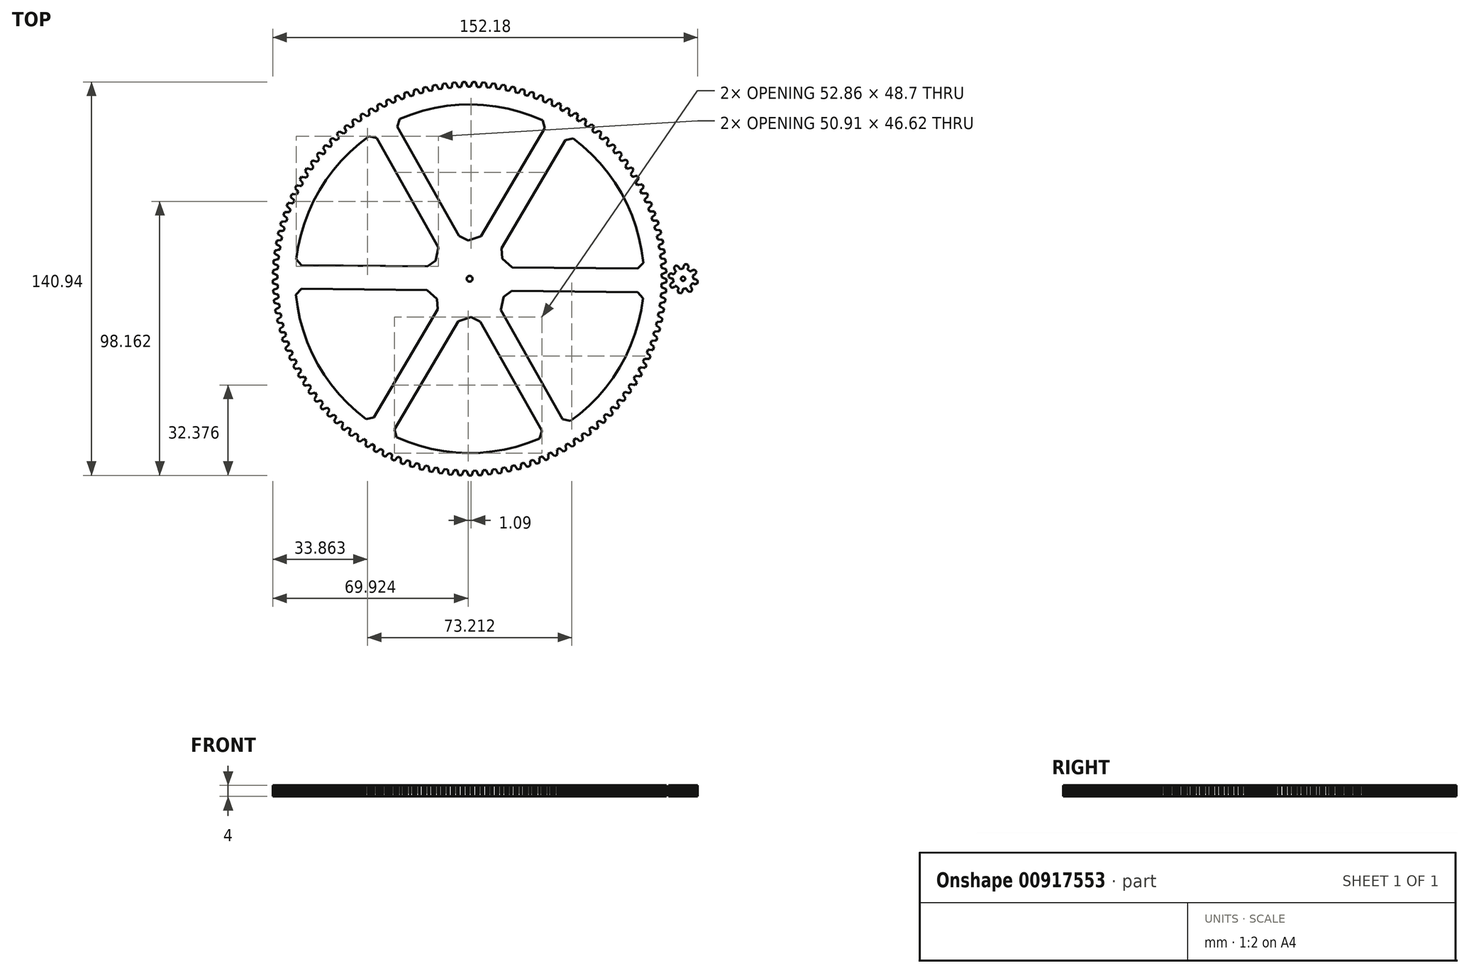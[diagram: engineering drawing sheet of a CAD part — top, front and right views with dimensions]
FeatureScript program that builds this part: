
annotation { "Feature Type Name" : "Feature", "Feature Type Description" : "" }
export const myFeature = defineFeature(function(context is Context, id is Id, definition is map)
    precondition{}
    {
        {
            var Q0;
            Q0=qCreatedBy(makeId("Top.planeOp"),FACE);
            var sketch = newSketch(context, id + "F0", { "sketchPlane" : qUnion([Q0])});
            skLineSegment(sketch, "E0", {"start": v(63.17, 0.46) * mm, "end": v(63.59, 0.33) * mm});
            skLineSegment(sketch, "E1", {"start": v(63.59, 0.33) * mm, "end": v(64.43, 0.02) * mm});
            skLineSegment(sketch, "E2", {"start": v(64.43, 0.02) * mm, "end": v(64.85, -0.14) * mm});
            skLineSegment(sketch, "E3", {"start": v(64.85, -0.14) * mm, "end": v(64.84, -1.27) * mm});
            skLineSegment(sketch, "E4", {"start": v(64.84, -1.27) * mm, "end": v(64.41, -1.42) * mm});
            skLineSegment(sketch, "E5", {"start": v(64.41, -1.42) * mm, "end": v(63.57, -1.71) * mm});
            skLineSegment(sketch, "E6", {"start": v(63.57, -1.71) * mm, "end": v(63.14, -1.84) * mm});
            skLineSegment(sketch, "E7", {"start": v(63.14, -1.84) * mm, "end": v(63.1, -3) * mm});
            skLineSegment(sketch, "E8", {"start": v(63.1, -3) * mm, "end": v(63.52, -3.15) * mm});
            skLineSegment(sketch, "E9", {"start": v(63.52, -3.15) * mm, "end": v(64.34, -3.5) * mm});
            skLineSegment(sketch, "E10", {"start": v(64.34, -3.5) * mm, "end": v(64.75, -3.68) * mm});
            skLineSegment(sketch, "E11", {"start": v(64.75, -3.68) * mm, "end": v(64.68, -4.8) * mm});
            skLineSegment(sketch, "E12", {"start": v(64.68, -4.8) * mm, "end": v(64.25, -4.94) * mm});
            skLineSegment(sketch, "E13", {"start": v(64.25, -4.94) * mm, "end": v(63.4, -5.18) * mm});
            skLineSegment(sketch, "E14", {"start": v(63.4, -5.18) * mm, "end": v(62.97, -5.3) * mm});
            skLineSegment(sketch, "E15", {"start": v(62.97, -5.3) * mm, "end": v(62.87, -6.44) * mm});
            skLineSegment(sketch, "E16", {"start": v(62.87, -6.44) * mm, "end": v(63.27, -6.62) * mm});
            skLineSegment(sketch, "E17", {"start": v(63.27, -6.62) * mm, "end": v(64.08, -7) * mm});
            skLineSegment(sketch, "E18", {"start": v(64.08, -7) * mm, "end": v(64.48, -7.21) * mm});
            skLineSegment(sketch, "E19", {"start": v(64.48, -7.21) * mm, "end": v(64.35, -8.33) * mm});
            skLineSegment(sketch, "E20", {"start": v(64.35, -8.33) * mm, "end": v(63.92, -8.45) * mm});
            skLineSegment(sketch, "E21", {"start": v(63.92, -8.45) * mm, "end": v(63.05, -8.65) * mm});
            skLineSegment(sketch, "E22", {"start": v(63.05, -8.65) * mm, "end": v(62.61, -8.73) * mm});
            skLineSegment(sketch, "E23", {"start": v(62.61, -8.73) * mm, "end": v(62.46, -9.88) * mm});
            skLineSegment(sketch, "E24", {"start": v(62.46, -9.88) * mm, "end": v(62.85, -10.08) * mm});
            skLineSegment(sketch, "E25", {"start": v(62.85, -10.08) * mm, "end": v(63.64, -10.5) * mm});
            skLineSegment(sketch, "E26", {"start": v(63.64, -10.5) * mm, "end": v(64.03, -10.73) * mm});
            skLineSegment(sketch, "E27", {"start": v(64.03, -10.73) * mm, "end": v(63.85, -11.84) * mm});
            skLineSegment(sketch, "E28", {"start": v(63.85, -11.84) * mm, "end": v(63.4, -11.93) * mm});
            skLineSegment(sketch, "E29", {"start": v(63.4, -11.93) * mm, "end": v(62.53, -12.08) * mm});
            skLineSegment(sketch, "E30", {"start": v(62.53, -12.08) * mm, "end": v(62.09, -12.15) * mm});
            skLineSegment(sketch, "E31", {"start": v(62.09, -12.15) * mm, "end": v(61.87, -13.28) * mm});
            skLineSegment(sketch, "E32", {"start": v(61.87, -13.28) * mm, "end": v(62.26, -13.5) * mm});
            skLineSegment(sketch, "E33", {"start": v(62.26, -13.5) * mm, "end": v(63.02, -13.97) * mm});
            skLineSegment(sketch, "E34", {"start": v(63.02, -13.97) * mm, "end": v(63.4, -14.21) * mm});
            skLineSegment(sketch, "E35", {"start": v(63.4, -14.21) * mm, "end": v(63.16, -15.31) * mm});
            skLineSegment(sketch, "E36", {"start": v(63.16, -15.31) * mm, "end": v(62.72, -15.38) * mm});
            skLineSegment(sketch, "E37", {"start": v(62.72, -15.38) * mm, "end": v(61.83, -15.5) * mm});
            skLineSegment(sketch, "E38", {"start": v(61.83, -15.5) * mm, "end": v(61.4, -15.54) * mm});
            skLineSegment(sketch, "E39", {"start": v(61.4, -15.54) * mm, "end": v(61.12, -16.66) * mm});
            skLineSegment(sketch, "E40", {"start": v(61.12, -16.66) * mm, "end": v(61.5, -16.9) * mm});
            skLineSegment(sketch, "E41", {"start": v(61.5, -16.9) * mm, "end": v(62.23, -17.4) * mm});
            skLineSegment(sketch, "E42", {"start": v(62.23, -17.4) * mm, "end": v(62.6, -17.66) * mm});
            skLineSegment(sketch, "E43", {"start": v(62.6, -17.66) * mm, "end": v(62.3, -18.75) * mm});
            skLineSegment(sketch, "E44", {"start": v(62.3, -18.75) * mm, "end": v(61.86, -18.8) * mm});
            skLineSegment(sketch, "E45", {"start": v(61.86, -18.8) * mm, "end": v(60.97, -18.86) * mm});
            skLineSegment(sketch, "E46", {"start": v(60.97, -18.86) * mm, "end": v(60.53, -18.88) * mm});
            skLineSegment(sketch, "E47", {"start": v(60.53, -18.88) * mm, "end": v(60.2, -20) * mm});
            skLineSegment(sketch, "E48", {"start": v(60.2, -20) * mm, "end": v(60.56, -20.25) * mm});
            skLineSegment(sketch, "E49", {"start": v(60.56, -20.25) * mm, "end": v(61.27, -20.79) * mm});
            skLineSegment(sketch, "E50", {"start": v(61.27, -20.79) * mm, "end": v(61.62, -21.07) * mm});
            skLineSegment(sketch, "E51", {"start": v(61.62, -21.07) * mm, "end": v(61.28, -22.14) * mm});
            skLineSegment(sketch, "E52", {"start": v(61.28, -22.14) * mm, "end": v(60.83, -22.16) * mm});
            skLineSegment(sketch, "E53", {"start": v(60.83, -22.16) * mm, "end": v(59.94, -22.19) * mm});
            skLineSegment(sketch, "E54", {"start": v(59.94, -22.19) * mm, "end": v(59.5, -22.18) * mm});
            skLineSegment(sketch, "E55", {"start": v(59.5, -22.18) * mm, "end": v(59.11, -23.27) * mm});
            skLineSegment(sketch, "E56", {"start": v(59.11, -23.27) * mm, "end": v(59.46, -23.55) * mm});
            skLineSegment(sketch, "E57", {"start": v(59.46, -23.55) * mm, "end": v(60.14, -24.12) * mm});
            skLineSegment(sketch, "E58", {"start": v(60.14, -24.12) * mm, "end": v(60.48, -24.42) * mm});
            skLineSegment(sketch, "E59", {"start": v(60.48, -24.42) * mm, "end": v(60.08, -25.47) * mm});
            skLineSegment(sketch, "E60", {"start": v(60.08, -25.47) * mm, "end": v(59.63, -25.47) * mm});
            skLineSegment(sketch, "E61", {"start": v(59.63, -25.47) * mm, "end": v(58.74, -25.45) * mm});
            skLineSegment(sketch, "E62", {"start": v(58.74, -25.45) * mm, "end": v(58.3, -25.43) * mm});
            skLineSegment(sketch, "E63", {"start": v(58.3, -25.43) * mm, "end": v(57.86, -26.5) * mm});
            skLineSegment(sketch, "E64", {"start": v(57.86, -26.5) * mm, "end": v(58.2, -26.79) * mm});
            skLineSegment(sketch, "E65", {"start": v(58.2, -26.79) * mm, "end": v(58.85, -27.4) * mm});
            skLineSegment(sketch, "E66", {"start": v(58.85, -27.4) * mm, "end": v(59.17, -27.71) * mm});
            skLineSegment(sketch, "E67", {"start": v(59.17, -27.71) * mm, "end": v(58.72, -28.74) * mm});
            skLineSegment(sketch, "E68", {"start": v(58.72, -28.74) * mm, "end": v(58.27, -28.72) * mm});
            skLineSegment(sketch, "E69", {"start": v(58.27, -28.72) * mm, "end": v(57.38, -28.65) * mm});
            skLineSegment(sketch, "E70", {"start": v(57.38, -28.65) * mm, "end": v(56.94, -28.6) * mm});
            skLineSegment(sketch, "E71", {"start": v(56.94, -28.6) * mm, "end": v(56.45, -29.65) * mm});
            skLineSegment(sketch, "E72", {"start": v(56.45, -29.65) * mm, "end": v(56.77, -29.96) * mm});
            skLineSegment(sketch, "E73", {"start": v(56.77, -29.96) * mm, "end": v(57.4, -30.6) * mm});
            skLineSegment(sketch, "E74", {"start": v(57.4, -30.6) * mm, "end": v(57.7, -30.93) * mm});
            skLineSegment(sketch, "E75", {"start": v(57.7, -30.93) * mm, "end": v(57.2, -31.94) * mm});
            skLineSegment(sketch, "E76", {"start": v(57.2, -31.94) * mm, "end": v(56.75, -31.9) * mm});
            skLineSegment(sketch, "E77", {"start": v(56.75, -31.9) * mm, "end": v(55.86, -31.78) * mm});
            skLineSegment(sketch, "E78", {"start": v(55.86, -31.78) * mm, "end": v(55.42, -31.71) * mm});
            skLineSegment(sketch, "E79", {"start": v(55.42, -31.71) * mm, "end": v(54.88, -32.73) * mm});
            skLineSegment(sketch, "E80", {"start": v(54.88, -32.73) * mm, "end": v(55.18, -33.06) * mm});
            skLineSegment(sketch, "E81", {"start": v(55.18, -33.06) * mm, "end": v(55.77, -33.73) * mm});
            skLineSegment(sketch, "E82", {"start": v(55.77, -33.73) * mm, "end": v(56.06, -34.07) * mm});
            skLineSegment(sketch, "E83", {"start": v(56.06, -34.07) * mm, "end": v(55.5, -35.05) * mm});
            skLineSegment(sketch, "E84", {"start": v(55.5, -35.05) * mm, "end": v(55.06, -34.99) * mm});
            skLineSegment(sketch, "E85", {"start": v(55.06, -34.99) * mm, "end": v(54.18, -34.83) * mm});
            skLineSegment(sketch, "E86", {"start": v(54.18, -34.83) * mm, "end": v(53.75, -34.74) * mm});
            skLineSegment(sketch, "E87", {"start": v(53.75, -34.74) * mm, "end": v(53.16, -35.73) * mm});
            skLineSegment(sketch, "E88", {"start": v(53.16, -35.73) * mm, "end": v(53.45, -36.07) * mm});
            skLineSegment(sketch, "E89", {"start": v(53.45, -36.07) * mm, "end": v(54, -36.77) * mm});
            skLineSegment(sketch, "E90", {"start": v(54, -36.77) * mm, "end": v(54.27, -37.13) * mm});
            skLineSegment(sketch, "E91", {"start": v(54.27, -37.13) * mm, "end": v(53.67, -38.08) * mm});
            skLineSegment(sketch, "E92", {"start": v(53.67, -38.08) * mm, "end": v(53.23, -38) * mm});
            skLineSegment(sketch, "E93", {"start": v(53.23, -38) * mm, "end": v(52.36, -37.8) * mm});
            skLineSegment(sketch, "E94", {"start": v(52.36, -37.8) * mm, "end": v(51.93, -37.68) * mm});
            skLineSegment(sketch, "E95", {"start": v(51.93, -37.68) * mm, "end": v(51.3, -38.64) * mm});
            skLineSegment(sketch, "E96", {"start": v(51.3, -38.64) * mm, "end": v(51.56, -39) * mm});
            skLineSegment(sketch, "E97", {"start": v(51.56, -39) * mm, "end": v(52.08, -39.72) * mm});
            skLineSegment(sketch, "E98", {"start": v(52.08, -39.72) * mm, "end": v(52.33, -40.1) * mm});
            skLineSegment(sketch, "E99", {"start": v(52.33, -40.1) * mm, "end": v(51.68, -41.01) * mm});
            skLineSegment(sketch, "E100", {"start": v(51.68, -41.01) * mm, "end": v(51.25, -40.9) * mm});
            skLineSegment(sketch, "E101", {"start": v(51.25, -40.9) * mm, "end": v(50.39, -40.66) * mm});
            skLineSegment(sketch, "E102", {"start": v(50.39, -40.66) * mm, "end": v(49.96, -40.52) * mm});
            skLineSegment(sketch, "E103", {"start": v(49.96, -40.52) * mm, "end": v(49.28, -41.45) * mm});
            skLineSegment(sketch, "E104", {"start": v(49.28, -41.45) * mm, "end": v(49.53, -41.82) * mm});
            skLineSegment(sketch, "E105", {"start": v(49.53, -41.82) * mm, "end": v(50, -42.57) * mm});
            skLineSegment(sketch, "E106", {"start": v(50, -42.57) * mm, "end": v(50.24, -42.95) * mm});
            skLineSegment(sketch, "E107", {"start": v(50.24, -42.95) * mm, "end": v(49.55, -43.84) * mm});
            skLineSegment(sketch, "E108", {"start": v(49.55, -43.84) * mm, "end": v(49.12, -43.7) * mm});
            skLineSegment(sketch, "E109", {"start": v(49.12, -43.7) * mm, "end": v(48.27, -43.42) * mm});
            skLineSegment(sketch, "E110", {"start": v(48.27, -43.42) * mm, "end": v(47.86, -43.27) * mm});
            skLineSegment(sketch, "E111", {"start": v(47.86, -43.27) * mm, "end": v(47.12, -44.16) * mm});
            skLineSegment(sketch, "E112", {"start": v(47.12, -44.16) * mm, "end": v(47.36, -44.53) * mm});
            skLineSegment(sketch, "E113", {"start": v(47.36, -44.53) * mm, "end": v(47.8, -45.3) * mm});
            skLineSegment(sketch, "E114", {"start": v(47.8, -45.3) * mm, "end": v(48.01, -45.7) * mm});
            skLineSegment(sketch, "E115", {"start": v(48.01, -45.7) * mm, "end": v(47.28, -46.56) * mm});
            skLineSegment(sketch, "E116", {"start": v(47.28, -46.56) * mm, "end": v(46.85, -46.4) * mm});
            skLineSegment(sketch, "E117", {"start": v(46.85, -46.4) * mm, "end": v(46.02, -46.07) * mm});
            skLineSegment(sketch, "E118", {"start": v(46.02, -46.07) * mm, "end": v(45.62, -45.9) * mm});
            skLineSegment(sketch, "E119", {"start": v(45.62, -45.9) * mm, "end": v(44.84, -46.75) * mm});
            skLineSegment(sketch, "E120", {"start": v(44.84, -46.75) * mm, "end": v(45.05, -47.14) * mm});
            skLineSegment(sketch, "E121", {"start": v(45.05, -47.14) * mm, "end": v(45.46, -47.94) * mm});
            skLineSegment(sketch, "E122", {"start": v(45.46, -47.94) * mm, "end": v(45.65, -48.34) * mm});
            skLineSegment(sketch, "E123", {"start": v(45.65, -48.34) * mm, "end": v(44.87, -49.16) * mm});
            skLineSegment(sketch, "E124", {"start": v(44.87, -49.16) * mm, "end": v(44.46, -48.98) * mm});
            skLineSegment(sketch, "E125", {"start": v(44.46, -48.98) * mm, "end": v(43.64, -48.6) * mm});
            skLineSegment(sketch, "E126", {"start": v(43.64, -48.6) * mm, "end": v(43.25, -48.41) * mm});
            skLineSegment(sketch, "E127", {"start": v(43.25, -48.41) * mm, "end": v(42.43, -49.23) * mm});
            skLineSegment(sketch, "E128", {"start": v(42.43, -49.23) * mm, "end": v(42.62, -49.63) * mm});
            skLineSegment(sketch, "E129", {"start": v(42.62, -49.63) * mm, "end": v(42.98, -50.44) * mm});
            skLineSegment(sketch, "E130", {"start": v(42.98, -50.44) * mm, "end": v(43.16, -50.86) * mm});
            skLineSegment(sketch, "E131", {"start": v(43.16, -50.86) * mm, "end": v(42.34, -51.63) * mm});
            skLineSegment(sketch, "E132", {"start": v(42.34, -51.63) * mm, "end": v(41.93, -51.43) * mm});
            skLineSegment(sketch, "E133", {"start": v(41.93, -51.43) * mm, "end": v(41.14, -51.02) * mm});
            skLineSegment(sketch, "E134", {"start": v(41.14, -51.02) * mm, "end": v(40.75, -50.8) * mm});
            skLineSegment(sketch, "E135", {"start": v(40.75, -50.8) * mm, "end": v(39.9, -51.58) * mm});
            skLineSegment(sketch, "E136", {"start": v(39.9, -51.58) * mm, "end": v(40.06, -51.99) * mm});
            skLineSegment(sketch, "E137", {"start": v(40.06, -51.99) * mm, "end": v(40.39, -52.82) * mm});
            skLineSegment(sketch, "E138", {"start": v(40.39, -52.82) * mm, "end": v(40.54, -53.24) * mm});
            skLineSegment(sketch, "E139", {"start": v(40.54, -53.24) * mm, "end": v(39.68, -53.97) * mm});
            skLineSegment(sketch, "E140", {"start": v(39.68, -53.97) * mm, "end": v(39.29, -53.76) * mm});
            skLineSegment(sketch, "E141", {"start": v(39.29, -53.76) * mm, "end": v(38.52, -53.3) * mm});
            skLineSegment(sketch, "E142", {"start": v(38.52, -53.3) * mm, "end": v(38.14, -53.07) * mm});
            skLineSegment(sketch, "E143", {"start": v(38.14, -53.07) * mm, "end": v(37.24, -53.8) * mm});
            skLineSegment(sketch, "E144", {"start": v(37.24, -53.8) * mm, "end": v(37.4, -54.22) * mm});
            skLineSegment(sketch, "E145", {"start": v(37.4, -54.22) * mm, "end": v(37.67, -55.06) * mm});
            skLineSegment(sketch, "E146", {"start": v(37.67, -55.06) * mm, "end": v(37.8, -55.5) * mm});
            skLineSegment(sketch, "E147", {"start": v(37.8, -55.5) * mm, "end": v(36.91, -56.18) * mm});
            skLineSegment(sketch, "E148", {"start": v(36.91, -56.18) * mm, "end": v(36.53, -55.95) * mm});
            skLineSegment(sketch, "E149", {"start": v(36.53, -55.95) * mm, "end": v(35.78, -55.46) * mm});
            skLineSegment(sketch, "E150", {"start": v(35.78, -55.46) * mm, "end": v(35.42, -55.2) * mm});
            skLineSegment(sketch, "E151", {"start": v(35.42, -55.2) * mm, "end": v(34.49, -55.89) * mm});
            skLineSegment(sketch, "E152", {"start": v(34.49, -55.89) * mm, "end": v(34.62, -56.3) * mm});
            skLineSegment(sketch, "E153", {"start": v(34.62, -56.3) * mm, "end": v(34.85, -57.17) * mm});
            skLineSegment(sketch, "E154", {"start": v(34.85, -57.17) * mm, "end": v(34.96, -57.6) * mm});
            skLineSegment(sketch, "E155", {"start": v(34.96, -57.6) * mm, "end": v(34.04, -58.25) * mm});
            skLineSegment(sketch, "E156", {"start": v(34.04, -58.25) * mm, "end": v(33.66, -58) * mm});
            skLineSegment(sketch, "E157", {"start": v(33.66, -58) * mm, "end": v(32.94, -57.47) * mm});
            skLineSegment(sketch, "E158", {"start": v(32.94, -57.47) * mm, "end": v(32.6, -57.2) * mm});
            skLineSegment(sketch, "E159", {"start": v(32.6, -57.2) * mm, "end": v(31.63, -57.83) * mm});
            skLineSegment(sketch, "E160", {"start": v(31.63, -57.83) * mm, "end": v(31.74, -58.26) * mm});
            skLineSegment(sketch, "E161", {"start": v(31.74, -58.26) * mm, "end": v(31.93, -59.13) * mm});
            skLineSegment(sketch, "E162", {"start": v(31.93, -59.13) * mm, "end": v(32.02, -59.57) * mm});
            skLineSegment(sketch, "E163", {"start": v(32.02, -59.57) * mm, "end": v(31.06, -60.17) * mm});
            skLineSegment(sketch, "E164", {"start": v(31.06, -60.17) * mm, "end": v(30.7, -59.9) * mm});
            skLineSegment(sketch, "E165", {"start": v(30.7, -59.9) * mm, "end": v(30, -59.33) * mm});
            skLineSegment(sketch, "E166", {"start": v(30, -59.33) * mm, "end": v(29.67, -59.05) * mm});
            skLineSegment(sketch, "E167", {"start": v(29.67, -59.05) * mm, "end": v(28.67, -59.63) * mm});
            skLineSegment(sketch, "E168", {"start": v(28.67, -59.63) * mm, "end": v(28.76, -60.06) * mm});
            skLineSegment(sketch, "E169", {"start": v(28.76, -60.06) * mm, "end": v(28.91, -60.94) * mm});
            skLineSegment(sketch, "E170", {"start": v(28.91, -60.94) * mm, "end": v(28.97, -61.4) * mm});
            skLineSegment(sketch, "E171", {"start": v(28.97, -61.4) * mm, "end": v(27.99, -61.93) * mm});
            skLineSegment(sketch, "E172", {"start": v(27.99, -61.93) * mm, "end": v(27.65, -61.64) * mm});
            skLineSegment(sketch, "E173", {"start": v(27.65, -61.64) * mm, "end": v(26.98, -61.05) * mm});
            skLineSegment(sketch, "E174", {"start": v(26.98, -61.05) * mm, "end": v(26.66, -60.74) * mm});
            skLineSegment(sketch, "E175", {"start": v(26.66, -60.74) * mm, "end": v(25.63, -61.28) * mm});
            skLineSegment(sketch, "E176", {"start": v(25.63, -61.28) * mm, "end": v(25.7, -61.71) * mm});
            skLineSegment(sketch, "E177", {"start": v(25.7, -61.71) * mm, "end": v(25.8, -62.6) * mm});
            skLineSegment(sketch, "E178", {"start": v(25.8, -62.6) * mm, "end": v(25.85, -63.05) * mm});
            skLineSegment(sketch, "E179", {"start": v(25.85, -63.05) * mm, "end": v(24.84, -63.55) * mm});
            skLineSegment(sketch, "E180", {"start": v(24.84, -63.55) * mm, "end": v(24.5, -63.24) * mm});
            skLineSegment(sketch, "E181", {"start": v(24.5, -63.24) * mm, "end": v(23.87, -62.6) * mm});
            skLineSegment(sketch, "E182", {"start": v(23.87, -62.6) * mm, "end": v(23.56, -62.29) * mm});
            skLineSegment(sketch, "E183", {"start": v(23.56, -62.29) * mm, "end": v(22.52, -62.77) * mm});
            skLineSegment(sketch, "E184", {"start": v(22.52, -62.77) * mm, "end": v(22.56, -63.21) * mm});
            skLineSegment(sketch, "E185", {"start": v(22.56, -63.21) * mm, "end": v(22.62, -64.1) * mm});
            skLineSegment(sketch, "E186", {"start": v(22.62, -64.1) * mm, "end": v(22.64, -64.55) * mm});
            skLineSegment(sketch, "E187", {"start": v(22.64, -64.55) * mm, "end": v(21.6, -65) * mm});
            skLineSegment(sketch, "E188", {"start": v(21.6, -65) * mm, "end": v(21.3, -64.67) * mm});
            skLineSegment(sketch, "E189", {"start": v(21.3, -64.67) * mm, "end": v(20.69, -64.01) * mm});
            skLineSegment(sketch, "E190", {"start": v(20.69, -64.01) * mm, "end": v(20.4, -63.68) * mm});
            skLineSegment(sketch, "E191", {"start": v(20.4, -63.68) * mm, "end": v(19.33, -64.1) * mm});
            skLineSegment(sketch, "E192", {"start": v(19.33, -64.1) * mm, "end": v(19.35, -64.55) * mm});
            skLineSegment(sketch, "E193", {"start": v(19.35, -64.55) * mm, "end": v(19.36, -65.44) * mm});
            skLineSegment(sketch, "E194", {"start": v(19.36, -65.44) * mm, "end": v(19.36, -65.9) * mm});
            skLineSegment(sketch, "E195", {"start": v(19.36, -65.9) * mm, "end": v(18.3, -66.28) * mm});
            skLineSegment(sketch, "E196", {"start": v(18.3, -66.28) * mm, "end": v(18, -65.94) * mm});
            skLineSegment(sketch, "E197", {"start": v(18, -65.94) * mm, "end": v(17.44, -65.25) * mm});
            skLineSegment(sketch, "E198", {"start": v(17.44, -65.25) * mm, "end": v(17.17, -64.9) * mm});
            skLineSegment(sketch, "E199", {"start": v(17.17, -64.9) * mm, "end": v(16.07, -65.28) * mm});
            skLineSegment(sketch, "E200", {"start": v(16.07, -65.28) * mm, "end": v(16.07, -65.72) * mm});
            skLineSegment(sketch, "E201", {"start": v(16.07, -65.72) * mm, "end": v(16.04, -66.61) * mm});
            skLineSegment(sketch, "E202", {"start": v(16.04, -66.61) * mm, "end": v(16.02, -67.06) * mm});
            skLineSegment(sketch, "E203", {"start": v(16.02, -67.06) * mm, "end": v(14.94, -67.4) * mm});
            skLineSegment(sketch, "E204", {"start": v(14.94, -67.4) * mm, "end": v(14.66, -67.05) * mm});
            skLineSegment(sketch, "E205", {"start": v(14.66, -67.05) * mm, "end": v(14.13, -66.33) * mm});
            skLineSegment(sketch, "E206", {"start": v(14.13, -66.33) * mm, "end": v(13.88, -65.97) * mm});
            skLineSegment(sketch, "E207", {"start": v(13.88, -65.97) * mm, "end": v(12.77, -66.28) * mm});
            skLineSegment(sketch, "E208", {"start": v(12.77, -66.28) * mm, "end": v(12.74, -66.73) * mm});
            skLineSegment(sketch, "E209", {"start": v(12.74, -66.73) * mm, "end": v(12.67, -67.62) * mm});
            skLineSegment(sketch, "E210", {"start": v(12.67, -67.62) * mm, "end": v(12.62, -68.07) * mm});
            skLineSegment(sketch, "E211", {"start": v(12.62, -68.07) * mm, "end": v(11.53, -68.35) * mm});
            skLineSegment(sketch, "E212", {"start": v(11.53, -68.35) * mm, "end": v(11.27, -67.98) * mm});
            skLineSegment(sketch, "E213", {"start": v(11.27, -67.98) * mm, "end": v(10.77, -67.24) * mm});
            skLineSegment(sketch, "E214", {"start": v(10.77, -67.24) * mm, "end": v(10.54, -66.86) * mm});
            skLineSegment(sketch, "E215", {"start": v(10.54, -66.86) * mm, "end": v(9.41, -67.12) * mm});
            skLineSegment(sketch, "E216", {"start": v(9.41, -67.12) * mm, "end": v(9.37, -67.56) * mm});
            skLineSegment(sketch, "E217", {"start": v(9.37, -67.56) * mm, "end": v(9.25, -68.45) * mm});
            skLineSegment(sketch, "E218", {"start": v(9.25, -68.45) * mm, "end": v(9.18, -68.9) * mm});
            skLineSegment(sketch, "E219", {"start": v(9.18, -68.9) * mm, "end": v(8.07, -69.12) * mm});
            skLineSegment(sketch, "E220", {"start": v(8.07, -69.12) * mm, "end": v(7.83, -68.74) * mm});
            skLineSegment(sketch, "E221", {"start": v(7.83, -68.74) * mm, "end": v(7.37, -67.98) * mm});
            skLineSegment(sketch, "E222", {"start": v(7.37, -67.98) * mm, "end": v(7.16, -67.6) * mm});
            skLineSegment(sketch, "E223", {"start": v(7.16, -67.6) * mm, "end": v(6.02, -67.8) * mm});
            skLineSegment(sketch, "E224", {"start": v(6.02, -67.8) * mm, "end": v(5.95, -68.23) * mm});
            skLineSegment(sketch, "E225", {"start": v(5.95, -68.23) * mm, "end": v(5.8, -69.11) * mm});
            skLineSegment(sketch, "E226", {"start": v(5.8, -69.11) * mm, "end": v(5.7, -69.55) * mm});
            skLineSegment(sketch, "E227", {"start": v(5.7, -69.55) * mm, "end": v(4.58, -69.72) * mm});
            skLineSegment(sketch, "E228", {"start": v(4.58, -69.72) * mm, "end": v(4.36, -69.33) * mm});
            skLineSegment(sketch, "E229", {"start": v(4.36, -69.33) * mm, "end": v(3.94, -68.54) * mm});
            skLineSegment(sketch, "E230", {"start": v(3.94, -68.54) * mm, "end": v(3.74, -68.15) * mm});
            skLineSegment(sketch, "E231", {"start": v(3.74, -68.15) * mm, "end": v(2.6, -68.3) * mm});
            skLineSegment(sketch, "E232", {"start": v(2.6, -68.3) * mm, "end": v(2.5, -68.73) * mm});
            skLineSegment(sketch, "E233", {"start": v(2.5, -68.73) * mm, "end": v(2.3, -69.6) * mm});
            skLineSegment(sketch, "E234", {"start": v(2.3, -69.6) * mm, "end": v(2.19, -70.03) * mm});
            skLineSegment(sketch, "E235", {"start": v(2.19, -70.03) * mm, "end": v(1.07, -70.15) * mm});
            skLineSegment(sketch, "E236", {"start": v(1.07, -70.15) * mm, "end": v(0.86, -69.75) * mm});
            skLineSegment(sketch, "E237", {"start": v(0.86, -69.75) * mm, "end": v(0.48, -68.94) * mm});
            skLineSegment(sketch, "E238", {"start": v(0.48, -68.94) * mm, "end": v(0.3, -68.53) * mm});
            skLineSegment(sketch, "E239", {"start": v(0.3, -68.53) * mm, "end": v(-0.84, -68.62) * mm});
            skLineSegment(sketch, "E240", {"start": v(-0.84, -68.62) * mm, "end": v(-0.95, -69.05) * mm});
            skLineSegment(sketch, "E241", {"start": v(-0.95, -69.05) * mm, "end": v(-1.2, -69.9) * mm});
            skLineSegment(sketch, "E242", {"start": v(-1.2, -69.9) * mm, "end": v(-1.34, -70.34) * mm});
            skLineSegment(sketch, "E243", {"start": v(-1.34, -70.34) * mm, "end": v(-2.47, -70.4) * mm});
            skLineSegment(sketch, "E244", {"start": v(-2.47, -70.4) * mm, "end": v(-2.65, -69.98) * mm});
            skLineSegment(sketch, "E245", {"start": v(-2.65, -69.98) * mm, "end": v(-2.99, -69.16) * mm});
            skLineSegment(sketch, "E246", {"start": v(-2.99, -69.16) * mm, "end": v(-3.14, -68.74) * mm});
            skLineSegment(sketch, "E247", {"start": v(-3.14, -68.74) * mm, "end": v(-4.3, -68.77) * mm});
            skLineSegment(sketch, "E248", {"start": v(-4.3, -68.77) * mm, "end": v(-4.43, -69.2) * mm});
            skLineSegment(sketch, "E249", {"start": v(-4.43, -69.2) * mm, "end": v(-4.72, -70.04) * mm});
            skLineSegment(sketch, "E250", {"start": v(-4.72, -70.04) * mm, "end": v(-4.88, -70.46) * mm});
            skLineSegment(sketch, "E251", {"start": v(-4.88, -70.46) * mm, "end": v(-6, -70.47) * mm});
            skLineSegment(sketch, "E252", {"start": v(-6, -70.47) * mm, "end": v(-6.17, -70.04) * mm});
            skLineSegment(sketch, "E253", {"start": v(-6.17, -70.04) * mm, "end": v(-6.47, -69.2) * mm});
            skLineSegment(sketch, "E254", {"start": v(-6.47, -69.2) * mm, "end": v(-6.6, -68.78) * mm});
            skLineSegment(sketch, "E255", {"start": v(-6.6, -68.78) * mm, "end": v(-7.75, -68.75) * mm});
            skLineSegment(sketch, "E256", {"start": v(-7.75, -68.75) * mm, "end": v(-7.9, -69.17) * mm});
            skLineSegment(sketch, "E257", {"start": v(-7.9, -69.17) * mm, "end": v(-8.24, -70) * mm});
            skLineSegment(sketch, "E258", {"start": v(-8.24, -70) * mm, "end": v(-8.42, -70.41) * mm});
            skLineSegment(sketch, "E259", {"start": v(-8.42, -70.41) * mm, "end": v(-9.55, -70.36) * mm});
            skLineSegment(sketch, "E260", {"start": v(-9.55, -70.36) * mm, "end": v(-9.69, -69.93) * mm});
            skLineSegment(sketch, "E261", {"start": v(-9.69, -69.93) * mm, "end": v(-9.94, -69.07) * mm});
            skLineSegment(sketch, "E262", {"start": v(-9.94, -69.07) * mm, "end": v(-10.05, -68.64) * mm});
            skLineSegment(sketch, "E263", {"start": v(-10.05, -68.64) * mm, "end": v(-11.2, -68.56) * mm});
            skLineSegment(sketch, "E264", {"start": v(-11.2, -68.56) * mm, "end": v(-11.38, -68.97) * mm});
            skLineSegment(sketch, "E265", {"start": v(-11.38, -68.97) * mm, "end": v(-11.76, -69.78) * mm});
            skLineSegment(sketch, "E266", {"start": v(-11.76, -69.78) * mm, "end": v(-11.96, -70.18) * mm});
            skLineSegment(sketch, "E267", {"start": v(-11.96, -70.18) * mm, "end": v(-13.08, -70.07) * mm});
            skLineSegment(sketch, "E268", {"start": v(-13.08, -70.07) * mm, "end": v(-13.2, -69.64) * mm});
            skLineSegment(sketch, "E269", {"start": v(-13.2, -69.64) * mm, "end": v(-13.4, -68.77) * mm});
            skLineSegment(sketch, "E270", {"start": v(-13.4, -68.77) * mm, "end": v(-13.5, -68.33) * mm});
            skLineSegment(sketch, "E271", {"start": v(-13.5, -68.33) * mm, "end": v(-14.64, -68.2) * mm});
            skLineSegment(sketch, "E272", {"start": v(-14.64, -68.2) * mm, "end": v(-14.84, -68.6) * mm});
            skLineSegment(sketch, "E273", {"start": v(-14.84, -68.6) * mm, "end": v(-15.25, -69.38) * mm});
            skLineSegment(sketch, "E274", {"start": v(-15.25, -69.38) * mm, "end": v(-15.48, -69.77) * mm});
            skLineSegment(sketch, "E275", {"start": v(-15.48, -69.77) * mm, "end": v(-16.59, -69.6) * mm});
            skLineSegment(sketch, "E276", {"start": v(-16.59, -69.6) * mm, "end": v(-16.68, -69.17) * mm});
            skLineSegment(sketch, "E277", {"start": v(-16.68, -69.17) * mm, "end": v(-16.85, -68.29) * mm});
            skLineSegment(sketch, "E278", {"start": v(-16.85, -68.29) * mm, "end": v(-16.92, -67.85) * mm});
            skLineSegment(sketch, "E279", {"start": v(-16.92, -67.85) * mm, "end": v(-18.06, -67.65) * mm});
            skLineSegment(sketch, "E280", {"start": v(-18.06, -67.65) * mm, "end": v(-18.27, -68.04) * mm});
            skLineSegment(sketch, "E281", {"start": v(-18.27, -68.04) * mm, "end": v(-18.73, -68.8) * mm});
            skLineSegment(sketch, "E282", {"start": v(-18.73, -68.8) * mm, "end": v(-18.97, -69.2) * mm});
            skLineSegment(sketch, "E283", {"start": v(-18.97, -69.2) * mm, "end": v(-20.07, -68.97) * mm});
            skLineSegment(sketch, "E284", {"start": v(-20.07, -68.97) * mm, "end": v(-20.15, -68.52) * mm});
            skLineSegment(sketch, "E285", {"start": v(-20.15, -68.52) * mm, "end": v(-20.27, -67.64) * mm});
            skLineSegment(sketch, "E286", {"start": v(-20.27, -67.64) * mm, "end": v(-20.32, -67.2) * mm});
            skLineSegment(sketch, "E287", {"start": v(-20.32, -67.2) * mm, "end": v(-21.44, -66.94) * mm});
            skLineSegment(sketch, "E288", {"start": v(-21.44, -66.94) * mm, "end": v(-21.68, -67.32) * mm});
            skLineSegment(sketch, "E289", {"start": v(-21.68, -67.32) * mm, "end": v(-22.17, -68.06) * mm});
            skLineSegment(sketch, "E290", {"start": v(-22.17, -68.06) * mm, "end": v(-22.43, -68.43) * mm});
            skLineSegment(sketch, "E291", {"start": v(-22.43, -68.43) * mm, "end": v(-23.52, -68.16) * mm});
            skLineSegment(sketch, "E292", {"start": v(-23.52, -68.16) * mm, "end": v(-23.57, -67.7) * mm});
            skLineSegment(sketch, "E293", {"start": v(-23.57, -67.7) * mm, "end": v(-23.65, -66.82) * mm});
            skLineSegment(sketch, "E294", {"start": v(-23.65, -66.82) * mm, "end": v(-23.68, -66.38) * mm});
            skLineSegment(sketch, "E295", {"start": v(-23.68, -66.38) * mm, "end": v(-24.79, -66.06) * mm});
            skLineSegment(sketch, "E296", {"start": v(-24.79, -66.06) * mm, "end": v(-25.04, -66.43) * mm});
            skLineSegment(sketch, "E297", {"start": v(-25.04, -66.43) * mm, "end": v(-25.57, -67.15) * mm});
            skLineSegment(sketch, "E298", {"start": v(-25.57, -67.15) * mm, "end": v(-25.85, -67.5) * mm});
            skLineSegment(sketch, "E299", {"start": v(-25.85, -67.5) * mm, "end": v(-26.92, -67.17) * mm});
            skLineSegment(sketch, "E300", {"start": v(-26.92, -67.17) * mm, "end": v(-26.95, -66.72) * mm});
            skLineSegment(sketch, "E301", {"start": v(-26.95, -66.72) * mm, "end": v(-26.98, -65.83) * mm});
            skLineSegment(sketch, "E302", {"start": v(-26.98, -65.83) * mm, "end": v(-26.99, -65.39) * mm});
            skLineSegment(sketch, "E303", {"start": v(-26.99, -65.39) * mm, "end": v(-28.08, -65.02) * mm});
            skLineSegment(sketch, "E304", {"start": v(-28.08, -65.02) * mm, "end": v(-28.35, -65.37) * mm});
            skLineSegment(sketch, "E305", {"start": v(-28.35, -65.37) * mm, "end": v(-28.92, -66.06) * mm});
            skLineSegment(sketch, "E306", {"start": v(-28.92, -66.06) * mm, "end": v(-29.21, -66.4) * mm});
            skLineSegment(sketch, "E307", {"start": v(-29.21, -66.4) * mm, "end": v(-30.27, -66.02) * mm});
            skLineSegment(sketch, "E308", {"start": v(-30.27, -66.02) * mm, "end": v(-30.28, -65.56) * mm});
            skLineSegment(sketch, "E309", {"start": v(-30.28, -65.56) * mm, "end": v(-30.26, -64.67) * mm});
            skLineSegment(sketch, "E310", {"start": v(-30.26, -64.67) * mm, "end": v(-30.25, -64.23) * mm});
            skLineSegment(sketch, "E311", {"start": v(-30.25, -64.23) * mm, "end": v(-31.32, -63.8) * mm});
            skLineSegment(sketch, "E312", {"start": v(-31.32, -63.8) * mm, "end": v(-31.6, -64.14) * mm});
            skLineSegment(sketch, "E313", {"start": v(-31.6, -64.14) * mm, "end": v(-32.2, -64.8) * mm});
            skLineSegment(sketch, "E314", {"start": v(-32.2, -64.8) * mm, "end": v(-32.52, -65.13) * mm});
            skLineSegment(sketch, "E315", {"start": v(-32.52, -65.13) * mm, "end": v(-33.56, -64.7) * mm});
            skLineSegment(sketch, "E316", {"start": v(-33.56, -64.7) * mm, "end": v(-33.54, -64.24) * mm});
            skLineSegment(sketch, "E317", {"start": v(-33.54, -64.24) * mm, "end": v(-33.48, -63.35) * mm});
            skLineSegment(sketch, "E318", {"start": v(-33.48, -63.35) * mm, "end": v(-33.44, -62.91) * mm});
            skLineSegment(sketch, "E319", {"start": v(-33.44, -62.91) * mm, "end": v(-34.5, -62.44) * mm});
            skLineSegment(sketch, "E320", {"start": v(-34.5, -62.44) * mm, "end": v(-34.8, -62.76) * mm});
            skLineSegment(sketch, "E321", {"start": v(-34.8, -62.76) * mm, "end": v(-35.43, -63.39) * mm});
            skLineSegment(sketch, "E322", {"start": v(-35.43, -63.39) * mm, "end": v(-35.76, -63.7) * mm});
            skLineSegment(sketch, "E323", {"start": v(-35.76, -63.7) * mm, "end": v(-36.77, -63.2) * mm});
            skLineSegment(sketch, "E324", {"start": v(-36.77, -63.2) * mm, "end": v(-36.73, -62.76) * mm});
            skLineSegment(sketch, "E325", {"start": v(-36.73, -62.76) * mm, "end": v(-36.63, -61.87) * mm});
            skLineSegment(sketch, "E326", {"start": v(-36.63, -61.87) * mm, "end": v(-36.57, -61.43) * mm});
            skLineSegment(sketch, "E327", {"start": v(-36.57, -61.43) * mm, "end": v(-37.6, -60.9) * mm});
            skLineSegment(sketch, "E328", {"start": v(-37.6, -60.9) * mm, "end": v(-37.91, -61.21) * mm});
            skLineSegment(sketch, "E329", {"start": v(-37.91, -61.21) * mm, "end": v(-38.58, -61.81) * mm});
            skLineSegment(sketch, "E330", {"start": v(-38.58, -61.81) * mm, "end": v(-38.92, -62.1) * mm});
            skLineSegment(sketch, "E331", {"start": v(-38.92, -62.1) * mm, "end": v(-39.9, -61.56) * mm});
            skLineSegment(sketch, "E332", {"start": v(-39.9, -61.56) * mm, "end": v(-39.85, -61.12) * mm});
            skLineSegment(sketch, "E333", {"start": v(-39.85, -61.12) * mm, "end": v(-39.7, -60.24) * mm});
            skLineSegment(sketch, "E334", {"start": v(-39.7, -60.24) * mm, "end": v(-39.62, -59.8) * mm});
            skLineSegment(sketch, "E335", {"start": v(-39.62, -59.8) * mm, "end": v(-40.61, -59.22) * mm});
            skLineSegment(sketch, "E336", {"start": v(-40.61, -59.22) * mm, "end": v(-40.95, -59.51) * mm});
            skLineSegment(sketch, "E337", {"start": v(-40.95, -59.51) * mm, "end": v(-41.64, -60.08) * mm});
            skLineSegment(sketch, "E338", {"start": v(-41.64, -60.08) * mm, "end": v(-42, -60.35) * mm});
            skLineSegment(sketch, "E339", {"start": v(-42, -60.35) * mm, "end": v(-42.96, -59.76) * mm});
            skLineSegment(sketch, "E340", {"start": v(-42.96, -59.76) * mm, "end": v(-42.87, -59.32) * mm});
            skLineSegment(sketch, "E341", {"start": v(-42.87, -59.32) * mm, "end": v(-42.68, -58.45) * mm});
            skLineSegment(sketch, "E342", {"start": v(-42.68, -58.45) * mm, "end": v(-42.58, -58.02) * mm});
            skLineSegment(sketch, "E343", {"start": v(-42.58, -58.02) * mm, "end": v(-43.55, -57.39) * mm});
            skLineSegment(sketch, "E344", {"start": v(-43.55, -57.39) * mm, "end": v(-43.9, -57.66) * mm});
            skLineSegment(sketch, "E345", {"start": v(-43.9, -57.66) * mm, "end": v(-44.61, -58.2) * mm});
            skLineSegment(sketch, "E346", {"start": v(-44.61, -58.2) * mm, "end": v(-44.98, -58.45) * mm});
            skLineSegment(sketch, "E347", {"start": v(-44.98, -58.45) * mm, "end": v(-45.91, -57.81) * mm});
            skLineSegment(sketch, "E348", {"start": v(-45.91, -57.81) * mm, "end": v(-45.8, -57.37) * mm});
            skLineSegment(sketch, "E349", {"start": v(-45.8, -57.37) * mm, "end": v(-45.57, -56.51) * mm});
            skLineSegment(sketch, "E350", {"start": v(-45.57, -56.51) * mm, "end": v(-45.45, -56.09) * mm});
            skLineSegment(sketch, "E351", {"start": v(-45.45, -56.09) * mm, "end": v(-46.38, -55.41) * mm});
            skLineSegment(sketch, "E352", {"start": v(-46.38, -55.41) * mm, "end": v(-46.74, -55.67) * mm});
            skLineSegment(sketch, "E353", {"start": v(-46.74, -55.67) * mm, "end": v(-47.49, -56.16) * mm});
            skLineSegment(sketch, "E354", {"start": v(-47.49, -56.16) * mm, "end": v(-47.87, -56.4) * mm});
            skLineSegment(sketch, "E355", {"start": v(-47.87, -56.4) * mm, "end": v(-48.77, -55.71) * mm});
            skLineSegment(sketch, "E356", {"start": v(-48.77, -55.71) * mm, "end": v(-48.64, -55.28) * mm});
            skLineSegment(sketch, "E357", {"start": v(-48.64, -55.28) * mm, "end": v(-48.36, -54.43) * mm});
            skLineSegment(sketch, "E358", {"start": v(-48.36, -54.43) * mm, "end": v(-48.21, -54.02) * mm});
            skLineSegment(sketch, "E359", {"start": v(-48.21, -54.02) * mm, "end": v(-49.11, -53.3) * mm});
            skLineSegment(sketch, "E360", {"start": v(-49.11, -53.3) * mm, "end": v(-49.49, -53.53) * mm});
            skLineSegment(sketch, "E361", {"start": v(-49.49, -53.53) * mm, "end": v(-50.26, -53.98) * mm});
            skLineSegment(sketch, "E362", {"start": v(-50.26, -53.98) * mm, "end": v(-50.65, -54.2) * mm});
            skLineSegment(sketch, "E363", {"start": v(-50.65, -54.2) * mm, "end": v(-51.51, -53.48) * mm});
            skLineSegment(sketch, "E364", {"start": v(-51.51, -53.48) * mm, "end": v(-51.36, -53.05) * mm});
            skLineSegment(sketch, "E365", {"start": v(-51.36, -53.05) * mm, "end": v(-51.04, -52.22) * mm});
            skLineSegment(sketch, "E366", {"start": v(-51.04, -52.22) * mm, "end": v(-50.87, -51.8) * mm});
            skLineSegment(sketch, "E367", {"start": v(-50.87, -51.8) * mm, "end": v(-51.74, -51.04) * mm});
            skLineSegment(sketch, "E368", {"start": v(-51.74, -51.04) * mm, "end": v(-52.12, -51.26) * mm});
            skLineSegment(sketch, "E369", {"start": v(-52.12, -51.26) * mm, "end": v(-52.91, -51.67) * mm});
            skLineSegment(sketch, "E370", {"start": v(-52.91, -51.67) * mm, "end": v(-53.32, -51.87) * mm});
            skLineSegment(sketch, "E371", {"start": v(-53.32, -51.87) * mm, "end": v(-54.14, -51.1) * mm});
            skLineSegment(sketch, "E372", {"start": v(-54.14, -51.1) * mm, "end": v(-53.97, -50.69) * mm});
            skLineSegment(sketch, "E373", {"start": v(-53.97, -50.69) * mm, "end": v(-53.61, -49.87) * mm});
            skLineSegment(sketch, "E374", {"start": v(-53.61, -49.87) * mm, "end": v(-53.42, -49.47) * mm});
            skLineSegment(sketch, "E375", {"start": v(-53.42, -49.47) * mm, "end": v(-54.24, -48.66) * mm});
            skLineSegment(sketch, "E376", {"start": v(-54.24, -48.66) * mm, "end": v(-54.64, -48.86) * mm});
            skLineSegment(sketch, "E377", {"start": v(-54.64, -48.86) * mm, "end": v(-55.45, -49.23) * mm});
            skLineSegment(sketch, "E378", {"start": v(-55.45, -49.23) * mm, "end": v(-55.87, -49.4) * mm});
            skLineSegment(sketch, "E379", {"start": v(-55.87, -49.4) * mm, "end": v(-56.65, -48.6) * mm});
            skLineSegment(sketch, "E380", {"start": v(-56.65, -48.6) * mm, "end": v(-56.46, -48.2) * mm});
            skLineSegment(sketch, "E381", {"start": v(-56.46, -48.2) * mm, "end": v(-56.06, -47.4) * mm});
            skLineSegment(sketch, "E382", {"start": v(-56.06, -47.4) * mm, "end": v(-55.85, -47) * mm});
            skLineSegment(sketch, "E383", {"start": v(-55.85, -47) * mm, "end": v(-56.63, -46.15) * mm});
            skLineSegment(sketch, "E384", {"start": v(-56.63, -46.15) * mm, "end": v(-57.03, -46.33) * mm});
            skLineSegment(sketch, "E385", {"start": v(-57.03, -46.33) * mm, "end": v(-57.86, -46.67) * mm});
            skLineSegment(sketch, "E386", {"start": v(-57.86, -46.67) * mm, "end": v(-58.28, -46.82) * mm});
            skLineSegment(sketch, "E387", {"start": v(-58.28, -46.82) * mm, "end": v(-59.03, -45.97) * mm});
            skLineSegment(sketch, "E388", {"start": v(-59.03, -45.97) * mm, "end": v(-58.81, -45.58) * mm});
            skLineSegment(sketch, "E389", {"start": v(-58.81, -45.58) * mm, "end": v(-58.37, -44.8) * mm});
            skLineSegment(sketch, "E390", {"start": v(-58.37, -44.8) * mm, "end": v(-58.14, -44.42) * mm});
            skLineSegment(sketch, "E391", {"start": v(-58.14, -44.42) * mm, "end": v(-58.88, -43.53) * mm});
            skLineSegment(sketch, "E392", {"start": v(-58.88, -43.53) * mm, "end": v(-59.3, -43.69) * mm});
            skLineSegment(sketch, "E393", {"start": v(-59.3, -43.69) * mm, "end": v(-60.14, -43.98) * mm});
            skLineSegment(sketch, "E394", {"start": v(-60.14, -43.98) * mm, "end": v(-60.57, -44.12) * mm});
            skLineSegment(sketch, "E395", {"start": v(-60.57, -44.12) * mm, "end": v(-61.27, -43.23) * mm});
            skLineSegment(sketch, "E396", {"start": v(-61.27, -43.23) * mm, "end": v(-61.04, -42.85) * mm});
            skLineSegment(sketch, "E397", {"start": v(-61.04, -42.85) * mm, "end": v(-60.56, -42.1) * mm});
            skLineSegment(sketch, "E398", {"start": v(-60.56, -42.1) * mm, "end": v(-60.3, -41.73) * mm});
            skLineSegment(sketch, "E399", {"start": v(-60.3, -41.73) * mm, "end": v(-61, -40.8) * mm});
            skLineSegment(sketch, "E400", {"start": v(-61, -40.8) * mm, "end": v(-61.42, -40.94) * mm});
            skLineSegment(sketch, "E401", {"start": v(-61.42, -40.94) * mm, "end": v(-62.28, -41.19) * mm});
            skLineSegment(sketch, "E402", {"start": v(-62.28, -41.19) * mm, "end": v(-62.72, -41.3) * mm});
            skLineSegment(sketch, "E403", {"start": v(-62.72, -41.3) * mm, "end": v(-63.37, -40.38) * mm});
            skLineSegment(sketch, "E404", {"start": v(-63.37, -40.38) * mm, "end": v(-63.12, -40) * mm});
            skLineSegment(sketch, "E405", {"start": v(-63.12, -40) * mm, "end": v(-62.6, -39.28) * mm});
            skLineSegment(sketch, "E406", {"start": v(-62.6, -39.28) * mm, "end": v(-62.34, -38.93) * mm});
            skLineSegment(sketch, "E407", {"start": v(-62.34, -38.93) * mm, "end": v(-62.98, -37.97) * mm});
            skLineSegment(sketch, "E408", {"start": v(-62.98, -37.97) * mm, "end": v(-63.41, -38.08) * mm});
            skLineSegment(sketch, "E409", {"start": v(-63.41, -38.08) * mm, "end": v(-64.28, -38.29) * mm});
            skLineSegment(sketch, "E410", {"start": v(-64.28, -38.29) * mm, "end": v(-64.72, -38.38) * mm});
            skLineSegment(sketch, "E411", {"start": v(-64.72, -38.38) * mm, "end": v(-65.33, -37.43) * mm});
            skLineSegment(sketch, "E412", {"start": v(-65.33, -37.43) * mm, "end": v(-65.06, -37.07) * mm});
            skLineSegment(sketch, "E413", {"start": v(-65.06, -37.07) * mm, "end": v(-64.5, -36.37) * mm});
            skLineSegment(sketch, "E414", {"start": v(-64.5, -36.37) * mm, "end": v(-64.22, -36.03) * mm});
            skLineSegment(sketch, "E415", {"start": v(-64.22, -36.03) * mm, "end": v(-64.82, -35.04) * mm});
            skLineSegment(sketch, "E416", {"start": v(-64.82, -35.04) * mm, "end": v(-65.25, -35.13) * mm});
            skLineSegment(sketch, "E417", {"start": v(-65.25, -35.13) * mm, "end": v(-66.13, -35.3) * mm});
            skLineSegment(sketch, "E418", {"start": v(-66.13, -35.3) * mm, "end": v(-66.57, -35.36) * mm});
            skLineSegment(sketch, "E419", {"start": v(-66.57, -35.36) * mm, "end": v(-67.13, -34.38) * mm});
            skLineSegment(sketch, "E420", {"start": v(-67.13, -34.38) * mm, "end": v(-66.85, -34.04) * mm});
            skLineSegment(sketch, "E421", {"start": v(-66.85, -34.04) * mm, "end": v(-66.26, -33.36) * mm});
            skLineSegment(sketch, "E422", {"start": v(-66.26, -33.36) * mm, "end": v(-65.96, -33.04) * mm});
            skLineSegment(sketch, "E423", {"start": v(-65.96, -33.04) * mm, "end": v(-66.5, -32.02) * mm});
            skLineSegment(sketch, "E424", {"start": v(-66.5, -32.02) * mm, "end": v(-66.94, -32.1) * mm});
            skLineSegment(sketch, "E425", {"start": v(-66.94, -32.1) * mm, "end": v(-67.83, -32.2) * mm});
            skLineSegment(sketch, "E426", {"start": v(-67.83, -32.2) * mm, "end": v(-68.27, -32.25) * mm});
            skLineSegment(sketch, "E427", {"start": v(-68.27, -32.25) * mm, "end": v(-68.78, -31.25) * mm});
            skLineSegment(sketch, "E428", {"start": v(-68.78, -31.25) * mm, "end": v(-68.48, -30.92) * mm});
            skLineSegment(sketch, "E429", {"start": v(-68.48, -30.92) * mm, "end": v(-67.86, -30.27) * mm});
            skLineSegment(sketch, "E430", {"start": v(-67.86, -30.27) * mm, "end": v(-67.54, -29.96) * mm});
            skLineSegment(sketch, "E431", {"start": v(-67.54, -29.96) * mm, "end": v(-68.04, -28.92) * mm});
            skLineSegment(sketch, "E432", {"start": v(-68.04, -28.92) * mm, "end": v(-68.48, -28.97) * mm});
            skLineSegment(sketch, "E433", {"start": v(-68.48, -28.97) * mm, "end": v(-69.37, -29.04) * mm});
            skLineSegment(sketch, "E434", {"start": v(-69.37, -29.04) * mm, "end": v(-69.82, -29.07) * mm});
            skLineSegment(sketch, "E435", {"start": v(-69.82, -29.07) * mm, "end": v(-70.27, -28.04) * mm});
            skLineSegment(sketch, "E436", {"start": v(-70.27, -28.04) * mm, "end": v(-69.95, -27.72) * mm});
            skLineSegment(sketch, "E437", {"start": v(-69.95, -27.72) * mm, "end": v(-69.3, -27.1) * mm});
            skLineSegment(sketch, "E438", {"start": v(-69.3, -27.1) * mm, "end": v(-68.97, -26.81) * mm});
            skLineSegment(sketch, "E439", {"start": v(-68.97, -26.81) * mm, "end": v(-69.41, -25.75) * mm});
            skLineSegment(sketch, "E440", {"start": v(-69.41, -25.75) * mm, "end": v(-69.85, -25.77) * mm});
            skLineSegment(sketch, "E441", {"start": v(-69.85, -25.77) * mm, "end": v(-70.75, -25.8) * mm});
            skLineSegment(sketch, "E442", {"start": v(-70.75, -25.8) * mm, "end": v(-71.2, -25.8) * mm});
            skLineSegment(sketch, "E443", {"start": v(-71.2, -25.8) * mm, "end": v(-71.6, -24.75) * mm});
            skLineSegment(sketch, "E444", {"start": v(-71.6, -24.75) * mm, "end": v(-71.26, -24.45) * mm});
            skLineSegment(sketch, "E445", {"start": v(-71.26, -24.45) * mm, "end": v(-70.58, -23.87) * mm});
            skLineSegment(sketch, "E446", {"start": v(-70.58, -23.87) * mm, "end": v(-70.24, -23.6) * mm});
            skLineSegment(sketch, "E447", {"start": v(-70.24, -23.6) * mm, "end": v(-70.62, -22.51) * mm});
            skLineSegment(sketch, "E448", {"start": v(-70.62, -22.51) * mm, "end": v(-71.07, -22.51) * mm});
            skLineSegment(sketch, "E449", {"start": v(-71.07, -22.51) * mm, "end": v(-71.96, -22.5) * mm});
            skLineSegment(sketch, "E450", {"start": v(-71.96, -22.5) * mm, "end": v(-72.4, -22.48) * mm});
            skLineSegment(sketch, "E451", {"start": v(-72.4, -22.48) * mm, "end": v(-72.76, -21.4) * mm});
            skLineSegment(sketch, "E452", {"start": v(-72.76, -21.4) * mm, "end": v(-72.4, -21.12) * mm});
            skLineSegment(sketch, "E453", {"start": v(-72.4, -21.12) * mm, "end": v(-71.7, -20.58) * mm});
            skLineSegment(sketch, "E454", {"start": v(-71.7, -20.58) * mm, "end": v(-71.34, -20.32) * mm});
            skLineSegment(sketch, "E455", {"start": v(-71.34, -20.32) * mm, "end": v(-71.67, -19.22) * mm});
            skLineSegment(sketch, "E456", {"start": v(-71.67, -19.22) * mm, "end": v(-72.11, -19.2) * mm});
            skLineSegment(sketch, "E457", {"start": v(-72.11, -19.2) * mm, "end": v(-73, -19.14) * mm});
            skLineSegment(sketch, "E458", {"start": v(-73, -19.14) * mm, "end": v(-73.45, -19.1) * mm});
            skLineSegment(sketch, "E459", {"start": v(-73.45, -19.1) * mm, "end": v(-73.75, -18) * mm});
            skLineSegment(sketch, "E460", {"start": v(-73.75, -18) * mm, "end": v(-73.39, -17.74) * mm});
            skLineSegment(sketch, "E461", {"start": v(-73.39, -17.74) * mm, "end": v(-72.65, -17.23) * mm});
            skLineSegment(sketch, "E462", {"start": v(-72.65, -17.23) * mm, "end": v(-72.28, -17) * mm});
            skLineSegment(sketch, "E463", {"start": v(-72.28, -17) * mm, "end": v(-72.55, -15.87) * mm});
            skLineSegment(sketch, "E464", {"start": v(-72.55, -15.87) * mm, "end": v(-73, -15.83) * mm});
            skLineSegment(sketch, "E465", {"start": v(-73, -15.83) * mm, "end": v(-73.88, -15.73) * mm});
            skLineSegment(sketch, "E466", {"start": v(-73.88, -15.73) * mm, "end": v(-74.33, -15.66) * mm});
            skLineSegment(sketch, "E467", {"start": v(-74.33, -15.66) * mm, "end": v(-74.57, -14.56) * mm});
            skLineSegment(sketch, "E468", {"start": v(-74.57, -14.56) * mm, "end": v(-74.2, -14.31) * mm});
            skLineSegment(sketch, "E469", {"start": v(-74.2, -14.31) * mm, "end": v(-73.43, -13.84) * mm});
            skLineSegment(sketch, "E470", {"start": v(-73.43, -13.84) * mm, "end": v(-73.05, -13.62) * mm});
            skLineSegment(sketch, "E471", {"start": v(-73.05, -13.62) * mm, "end": v(-73.27, -12.49) * mm});
            skLineSegment(sketch, "E472", {"start": v(-73.27, -12.49) * mm, "end": v(-73.7, -12.43) * mm});
            skLineSegment(sketch, "E473", {"start": v(-73.7, -12.43) * mm, "end": v(-74.59, -12.28) * mm});
            skLineSegment(sketch, "E474", {"start": v(-74.59, -12.28) * mm, "end": v(-75.03, -12.19) * mm});
            skLineSegment(sketch, "E475", {"start": v(-75.03, -12.19) * mm, "end": v(-75.21, -11.08) * mm});
            skLineSegment(sketch, "E476", {"start": v(-75.21, -11.08) * mm, "end": v(-74.83, -10.85) * mm});
            skLineSegment(sketch, "E477", {"start": v(-74.83, -10.85) * mm, "end": v(-74.04, -10.42) * mm});
            skLineSegment(sketch, "E478", {"start": v(-74.04, -10.42) * mm, "end": v(-73.65, -10.22) * mm});
            skLineSegment(sketch, "E479", {"start": v(-73.65, -10.22) * mm, "end": v(-73.81, -9.08) * mm});
            skLineSegment(sketch, "E480", {"start": v(-73.81, -9.08) * mm, "end": v(-74.24, -9) * mm});
            skLineSegment(sketch, "E481", {"start": v(-74.24, -9) * mm, "end": v(-75.12, -8.8) * mm});
            skLineSegment(sketch, "E482", {"start": v(-75.12, -8.8) * mm, "end": v(-75.55, -8.68) * mm});
            skLineSegment(sketch, "E483", {"start": v(-75.55, -8.68) * mm, "end": v(-75.68, -7.57) * mm});
            skLineSegment(sketch, "E484", {"start": v(-75.68, -7.57) * mm, "end": v(-75.28, -7.36) * mm});
            skLineSegment(sketch, "E485", {"start": v(-75.28, -7.36) * mm, "end": v(-74.48, -6.97) * mm});
            skLineSegment(sketch, "E486", {"start": v(-74.48, -6.97) * mm, "end": v(-74.08, -6.79) * mm});
            skLineSegment(sketch, "E487", {"start": v(-74.08, -6.79) * mm, "end": v(-74.18, -5.64) * mm});
            skLineSegment(sketch, "E488", {"start": v(-74.18, -5.64) * mm, "end": v(-74.6, -5.53) * mm});
            skLineSegment(sketch, "E489", {"start": v(-74.6, -5.53) * mm, "end": v(-75.47, -5.3) * mm});
            skLineSegment(sketch, "E490", {"start": v(-75.47, -5.3) * mm, "end": v(-75.9, -5.16) * mm});
            skLineSegment(sketch, "E491", {"start": v(-75.9, -5.16) * mm, "end": v(-75.98, -4.04) * mm});
            skLineSegment(sketch, "E492", {"start": v(-75.98, -4.04) * mm, "end": v(-75.57, -3.85) * mm});
            skLineSegment(sketch, "E493", {"start": v(-75.57, -3.85) * mm, "end": v(-74.74, -3.5) * mm});
            skLineSegment(sketch, "E494", {"start": v(-74.74, -3.5) * mm, "end": v(-74.33, -3.34) * mm});
            skLineSegment(sketch, "E495", {"start": v(-74.33, -3.34) * mm, "end": v(-74.38, -2.19) * mm});
            skLineSegment(sketch, "E496", {"start": v(-74.38, -2.19) * mm, "end": v(-74.8, -2.06) * mm});
            skLineSegment(sketch, "E497", {"start": v(-74.8, -2.06) * mm, "end": v(-75.65, -1.78) * mm});
            skLineSegment(sketch, "E498", {"start": v(-75.65, -1.78) * mm, "end": v(-76.07, -1.62) * mm});
            skLineSegment(sketch, "E499", {"start": v(-76.07, -1.62) * mm, "end": v(-76.09, -0.5) * mm});
            skLineSegment(sketch, "E500", {"start": v(-76.09, -0.5) * mm, "end": v(-75.67, -0.33) * mm});
            skLineSegment(sketch, "E501", {"start": v(-75.67, -0.33) * mm, "end": v(-74.83, -0.02) * mm});
            skLineSegment(sketch, "E502", {"start": v(-74.83, -0.02) * mm, "end": v(-74.41, 0.12) * mm});
            skLineSegment(sketch, "E503", {"start": v(-74.41, 0.12) * mm, "end": v(-74.4, 1.27) * mm});
            skLineSegment(sketch, "E504", {"start": v(-74.4, 1.27) * mm, "end": v(-74.82, 1.42) * mm});
            skLineSegment(sketch, "E505", {"start": v(-74.82, 1.42) * mm, "end": v(-75.65, 1.74) * mm});
            skLineSegment(sketch, "E506", {"start": v(-75.65, 1.74) * mm, "end": v(-76.06, 1.92) * mm});
            skLineSegment(sketch, "E507", {"start": v(-76.06, 1.92) * mm, "end": v(-76.03, 3.04) * mm});
            skLineSegment(sketch, "E508", {"start": v(-76.03, 3.04) * mm, "end": v(-75.6, 3.2) * mm});
            skLineSegment(sketch, "E509", {"start": v(-75.6, 3.2) * mm, "end": v(-74.75, 3.46) * mm});
            skLineSegment(sketch, "E510", {"start": v(-74.75, 3.46) * mm, "end": v(-74.32, 3.57) * mm});
            skLineSegment(sketch, "E511", {"start": v(-74.32, 3.57) * mm, "end": v(-74.25, 4.73) * mm});
            skLineSegment(sketch, "E512", {"start": v(-74.25, 4.73) * mm, "end": v(-74.66, 4.9) * mm});
            skLineSegment(sketch, "E513", {"start": v(-74.66, 4.9) * mm, "end": v(-75.47, 5.26) * mm});
            skLineSegment(sketch, "E514", {"start": v(-75.47, 5.26) * mm, "end": v(-75.88, 5.46) * mm});
            skLineSegment(sketch, "E515", {"start": v(-75.88, 5.46) * mm, "end": v(-75.78, 6.58) * mm});
            skLineSegment(sketch, "E516", {"start": v(-75.78, 6.58) * mm, "end": v(-75.35, 6.7) * mm});
            skLineSegment(sketch, "E517", {"start": v(-75.35, 6.7) * mm, "end": v(-74.48, 6.92) * mm});
            skLineSegment(sketch, "E518", {"start": v(-74.48, 6.92) * mm, "end": v(-74.05, 7.02) * mm});
            skLineSegment(sketch, "E519", {"start": v(-74.05, 7.02) * mm, "end": v(-73.93, 8.17) * mm});
            skLineSegment(sketch, "E520", {"start": v(-73.93, 8.17) * mm, "end": v(-74.33, 8.36) * mm});
            skLineSegment(sketch, "E521", {"start": v(-74.33, 8.36) * mm, "end": v(-75.12, 8.76) * mm});
            skLineSegment(sketch, "E522", {"start": v(-75.12, 8.76) * mm, "end": v(-75.52, 8.98) * mm});
            skLineSegment(sketch, "E523", {"start": v(-75.52, 8.98) * mm, "end": v(-75.36, 10.1) * mm});
            skLineSegment(sketch, "E524", {"start": v(-75.36, 10.1) * mm, "end": v(-74.93, 10.2) * mm});
            skLineSegment(sketch, "E525", {"start": v(-74.93, 10.2) * mm, "end": v(-74.05, 10.38) * mm});
            skLineSegment(sketch, "E526", {"start": v(-74.05, 10.38) * mm, "end": v(-73.61, 10.45) * mm});
            skLineSegment(sketch, "E527", {"start": v(-73.61, 10.45) * mm, "end": v(-73.43, 11.59) * mm});
            skLineSegment(sketch, "E528", {"start": v(-73.43, 11.59) * mm, "end": v(-73.82, 11.8) * mm});
            skLineSegment(sketch, "E529", {"start": v(-73.82, 11.8) * mm, "end": v(-74.6, 12.25) * mm});
            skLineSegment(sketch, "E530", {"start": v(-74.6, 12.25) * mm, "end": v(-74.98, 12.48) * mm});
            skLineSegment(sketch, "E531", {"start": v(-74.98, 12.48) * mm, "end": v(-74.77, 13.59) * mm});
            skLineSegment(sketch, "E532", {"start": v(-74.77, 13.59) * mm, "end": v(-74.33, 13.67) * mm});
            skLineSegment(sketch, "E533", {"start": v(-74.33, 13.67) * mm, "end": v(-73.44, 13.8) * mm});
            skLineSegment(sketch, "E534", {"start": v(-73.44, 13.8) * mm, "end": v(-73, 13.85) * mm});
            skLineSegment(sketch, "E535", {"start": v(-73, 13.85) * mm, "end": v(-72.76, 14.98) * mm});
            skLineSegment(sketch, "E536", {"start": v(-72.76, 14.98) * mm, "end": v(-73.14, 15.21) * mm});
            skLineSegment(sketch, "E537", {"start": v(-73.14, 15.21) * mm, "end": v(-73.9, 15.7) * mm});
            skLineSegment(sketch, "E538", {"start": v(-73.9, 15.7) * mm, "end": v(-74.26, 15.95) * mm});
            skLineSegment(sketch, "E539", {"start": v(-74.26, 15.95) * mm, "end": v(-74, 17.04) * mm});
            skLineSegment(sketch, "E540", {"start": v(-74, 17.04) * mm, "end": v(-73.55, 17.1) * mm});
            skLineSegment(sketch, "E541", {"start": v(-73.55, 17.1) * mm, "end": v(-72.66, 17.2) * mm});
            skLineSegment(sketch, "E542", {"start": v(-72.66, 17.2) * mm, "end": v(-72.22, 17.22) * mm});
            skLineSegment(sketch, "E543", {"start": v(-72.22, 17.22) * mm, "end": v(-71.92, 18.34) * mm});
            skLineSegment(sketch, "E544", {"start": v(-71.92, 18.34) * mm, "end": v(-72.3, 18.58) * mm});
            skLineSegment(sketch, "E545", {"start": v(-72.3, 18.58) * mm, "end": v(-73.02, 19.1) * mm});
            skLineSegment(sketch, "E546", {"start": v(-73.02, 19.1) * mm, "end": v(-73.38, 19.38) * mm});
            skLineSegment(sketch, "E547", {"start": v(-73.38, 19.38) * mm, "end": v(-73.06, 20.46) * mm});
            skLineSegment(sketch, "E548", {"start": v(-73.06, 20.46) * mm, "end": v(-72.6, 20.5) * mm});
            skLineSegment(sketch, "E549", {"start": v(-72.6, 20.5) * mm, "end": v(-71.72, 20.54) * mm});
            skLineSegment(sketch, "E550", {"start": v(-71.72, 20.54) * mm, "end": v(-71.27, 20.55) * mm});
            skLineSegment(sketch, "E551", {"start": v(-71.27, 20.55) * mm, "end": v(-70.92, 21.64) * mm});
            skLineSegment(sketch, "E552", {"start": v(-70.92, 21.64) * mm, "end": v(-71.27, 21.91) * mm});
            skLineSegment(sketch, "E553", {"start": v(-71.27, 21.91) * mm, "end": v(-71.97, 22.47) * mm});
            skLineSegment(sketch, "E554", {"start": v(-71.97, 22.47) * mm, "end": v(-72.32, 22.76) * mm});
            skLineSegment(sketch, "E555", {"start": v(-72.32, 22.76) * mm, "end": v(-71.94, 23.82) * mm});
            skLineSegment(sketch, "E556", {"start": v(-71.94, 23.82) * mm, "end": v(-71.5, 23.83) * mm});
            skLineSegment(sketch, "E557", {"start": v(-71.5, 23.83) * mm, "end": v(-70.6, 23.83) * mm});
            skLineSegment(sketch, "E558", {"start": v(-70.6, 23.83) * mm, "end": v(-70.16, 23.82) * mm});
            skLineSegment(sketch, "E559", {"start": v(-70.16, 23.82) * mm, "end": v(-69.75, 24.9) * mm});
            skLineSegment(sketch, "E560", {"start": v(-69.75, 24.9) * mm, "end": v(-70.09, 25.18) * mm});
            skLineSegment(sketch, "E561", {"start": v(-70.09, 25.18) * mm, "end": v(-70.76, 25.77) * mm});
            skLineSegment(sketch, "E562", {"start": v(-70.76, 25.77) * mm, "end": v(-71.09, 26.08) * mm});
            skLineSegment(sketch, "E563", {"start": v(-71.09, 26.08) * mm, "end": v(-70.66, 27.12) * mm});
            skLineSegment(sketch, "E564", {"start": v(-70.66, 27.12) * mm, "end": v(-70.21, 27.11) * mm});
            skLineSegment(sketch, "E565", {"start": v(-70.21, 27.11) * mm, "end": v(-69.32, 27.07) * mm});
            skLineSegment(sketch, "E566", {"start": v(-69.32, 27.07) * mm, "end": v(-68.88, 27.03) * mm});
            skLineSegment(sketch, "E567", {"start": v(-68.88, 27.03) * mm, "end": v(-68.42, 28.09) * mm});
            skLineSegment(sketch, "E568", {"start": v(-68.42, 28.09) * mm, "end": v(-68.74, 28.39) * mm});
            skLineSegment(sketch, "E569", {"start": v(-68.74, 28.39) * mm, "end": v(-69.38, 29.01) * mm});
            skLineSegment(sketch, "E570", {"start": v(-69.38, 29.01) * mm, "end": v(-69.7, 29.34) * mm});
            skLineSegment(sketch, "E571", {"start": v(-69.7, 29.34) * mm, "end": v(-69.22, 30.36) * mm});
            skLineSegment(sketch, "E572", {"start": v(-69.22, 30.36) * mm, "end": v(-68.77, 30.32) * mm});
            skLineSegment(sketch, "E573", {"start": v(-68.77, 30.32) * mm, "end": v(-67.88, 30.23) * mm});
            skLineSegment(sketch, "E574", {"start": v(-67.88, 30.23) * mm, "end": v(-67.44, 30.18) * mm});
            skLineSegment(sketch, "E575", {"start": v(-67.44, 30.18) * mm, "end": v(-66.93, 31.2) * mm});
            skLineSegment(sketch, "E576", {"start": v(-66.93, 31.2) * mm, "end": v(-67.24, 31.52) * mm});
            skLineSegment(sketch, "E577", {"start": v(-67.24, 31.52) * mm, "end": v(-67.84, 32.18) * mm});
            skLineSegment(sketch, "E578", {"start": v(-67.84, 32.18) * mm, "end": v(-68.14, 32.52) * mm});
            skLineSegment(sketch, "E579", {"start": v(-68.14, 32.52) * mm, "end": v(-67.61, 33.51) * mm});
            skLineSegment(sketch, "E580", {"start": v(-67.61, 33.51) * mm, "end": v(-67.17, 33.46) * mm});
            skLineSegment(sketch, "E581", {"start": v(-67.17, 33.46) * mm, "end": v(-66.28, 33.32) * mm});
            skLineSegment(sketch, "E582", {"start": v(-66.28, 33.32) * mm, "end": v(-65.85, 33.24) * mm});
            skLineSegment(sketch, "E583", {"start": v(-65.85, 33.24) * mm, "end": v(-65.28, 34.25) * mm});
            skLineSegment(sketch, "E584", {"start": v(-65.28, 34.25) * mm, "end": v(-65.58, 34.58) * mm});
            skLineSegment(sketch, "E585", {"start": v(-65.58, 34.58) * mm, "end": v(-66.15, 35.27) * mm});
            skLineSegment(sketch, "E586", {"start": v(-66.15, 35.27) * mm, "end": v(-66.43, 35.62) * mm});
            skLineSegment(sketch, "E587", {"start": v(-66.43, 35.62) * mm, "end": v(-65.85, 36.59) * mm});
            skLineSegment(sketch, "E588", {"start": v(-65.85, 36.59) * mm, "end": v(-65.4, 36.5) * mm});
            skLineSegment(sketch, "E589", {"start": v(-65.4, 36.5) * mm, "end": v(-64.53, 36.33) * mm});
            skLineSegment(sketch, "E590", {"start": v(-64.53, 36.33) * mm, "end": v(-64.1, 36.23) * mm});
            skLineSegment(sketch, "E591", {"start": v(-64.1, 36.23) * mm, "end": v(-63.49, 37.2) * mm});
            skLineSegment(sketch, "E592", {"start": v(-63.49, 37.2) * mm, "end": v(-63.76, 37.55) * mm});
            skLineSegment(sketch, "E593", {"start": v(-63.76, 37.55) * mm, "end": v(-64.3, 38.26) * mm});
            skLineSegment(sketch, "E594", {"start": v(-64.3, 38.26) * mm, "end": v(-64.56, 38.63) * mm});
            skLineSegment(sketch, "E595", {"start": v(-64.56, 38.63) * mm, "end": v(-63.94, 39.57) * mm});
            skLineSegment(sketch, "E596", {"start": v(-63.94, 39.57) * mm, "end": v(-63.5, 39.47) * mm});
            skLineSegment(sketch, "E597", {"start": v(-63.5, 39.47) * mm, "end": v(-62.63, 39.24) * mm});
            skLineSegment(sketch, "E598", {"start": v(-62.63, 39.24) * mm, "end": v(-62.2, 39.12) * mm});
            skLineSegment(sketch, "E599", {"start": v(-62.2, 39.12) * mm, "end": v(-61.54, 40.06) * mm});
            skLineSegment(sketch, "E600", {"start": v(-61.54, 40.06) * mm, "end": v(-61.8, 40.42) * mm});
            skLineSegment(sketch, "E601", {"start": v(-61.8, 40.42) * mm, "end": v(-62.3, 41.16) * mm});
            skLineSegment(sketch, "E602", {"start": v(-62.3, 41.16) * mm, "end": v(-62.55, 41.54) * mm});
            skLineSegment(sketch, "E603", {"start": v(-62.55, 41.54) * mm, "end": v(-61.88, 42.45) * mm});
            skLineSegment(sketch, "E604", {"start": v(-61.88, 42.45) * mm, "end": v(-61.44, 42.32) * mm});
            skLineSegment(sketch, "E605", {"start": v(-61.44, 42.32) * mm, "end": v(-60.59, 42.06) * mm});
            skLineSegment(sketch, "E606", {"start": v(-60.59, 42.06) * mm, "end": v(-60.17, 41.91) * mm});
            skLineSegment(sketch, "E607", {"start": v(-60.17, 41.91) * mm, "end": v(-59.46, 42.82) * mm});
            skLineSegment(sketch, "E608", {"start": v(-59.46, 42.82) * mm, "end": v(-59.7, 43.2) * mm});
            skLineSegment(sketch, "E609", {"start": v(-59.7, 43.2) * mm, "end": v(-60.16, 43.96) * mm});
            skLineSegment(sketch, "E610", {"start": v(-60.16, 43.96) * mm, "end": v(-60.39, 44.35) * mm});
            skLineSegment(sketch, "E611", {"start": v(-60.39, 44.35) * mm, "end": v(-59.67, 45.22) * mm});
            skLineSegment(sketch, "E612", {"start": v(-59.67, 45.22) * mm, "end": v(-59.25, 45.08) * mm});
            skLineSegment(sketch, "E613", {"start": v(-59.25, 45.08) * mm, "end": v(-58.4, 44.77) * mm});
            skLineSegment(sketch, "E614", {"start": v(-58.4, 44.77) * mm, "end": v(-58, 44.6) * mm});
            skLineSegment(sketch, "E615", {"start": v(-58, 44.6) * mm, "end": v(-57.24, 45.47) * mm});
            skLineSegment(sketch, "E616", {"start": v(-57.24, 45.47) * mm, "end": v(-57.46, 45.86) * mm});
            skLineSegment(sketch, "E617", {"start": v(-57.46, 45.86) * mm, "end": v(-57.89, 46.64) * mm});
            skLineSegment(sketch, "E618", {"start": v(-57.89, 46.64) * mm, "end": v(-58.1, 47.05) * mm});
            skLineSegment(sketch, "E619", {"start": v(-58.1, 47.05) * mm, "end": v(-57.33, 47.88) * mm});
            skLineSegment(sketch, "E620", {"start": v(-57.33, 47.88) * mm, "end": v(-56.91, 47.71) * mm});
            skLineSegment(sketch, "E621", {"start": v(-56.91, 47.71) * mm, "end": v(-56.1, 47.36) * mm});
            skLineSegment(sketch, "E622", {"start": v(-56.1, 47.36) * mm, "end": v(-55.69, 47.18) * mm});
            skLineSegment(sketch, "E623", {"start": v(-55.69, 47.18) * mm, "end": v(-54.9, 48.01) * mm});
            skLineSegment(sketch, "E624", {"start": v(-54.9, 48.01) * mm, "end": v(-55.1, 48.4) * mm});
            skLineSegment(sketch, "E625", {"start": v(-55.1, 48.4) * mm, "end": v(-55.48, 49.21) * mm});
            skLineSegment(sketch, "E626", {"start": v(-55.48, 49.21) * mm, "end": v(-55.66, 49.62) * mm});
            skLineSegment(sketch, "E627", {"start": v(-55.66, 49.62) * mm, "end": v(-54.86, 50.42) * mm});
            skLineSegment(sketch, "E628", {"start": v(-54.86, 50.42) * mm, "end": v(-54.45, 50.23) * mm});
            skLineSegment(sketch, "E629", {"start": v(-54.45, 50.23) * mm, "end": v(-53.65, 49.84) * mm});
            skLineSegment(sketch, "E630", {"start": v(-53.65, 49.84) * mm, "end": v(-53.26, 49.63) * mm});
            skLineSegment(sketch, "E631", {"start": v(-53.26, 49.63) * mm, "end": v(-52.42, 50.43) * mm});
            skLineSegment(sketch, "E632", {"start": v(-52.42, 50.43) * mm, "end": v(-52.6, 50.83) * mm});
            skLineSegment(sketch, "E633", {"start": v(-52.6, 50.83) * mm, "end": v(-52.94, 51.65) * mm});
            skLineSegment(sketch, "E634", {"start": v(-52.94, 51.65) * mm, "end": v(-53.1, 52.07) * mm});
            skLineSegment(sketch, "E635", {"start": v(-53.1, 52.07) * mm, "end": v(-52.27, 52.83) * mm});
            skLineSegment(sketch, "E636", {"start": v(-52.27, 52.83) * mm, "end": v(-51.87, 52.62) * mm});
            skLineSegment(sketch, "E637", {"start": v(-51.87, 52.62) * mm, "end": v(-51.08, 52.19) * mm});
            skLineSegment(sketch, "E638", {"start": v(-51.08, 52.19) * mm, "end": v(-50.7, 51.96) * mm});
            skLineSegment(sketch, "E639", {"start": v(-50.7, 51.96) * mm, "end": v(-49.82, 52.71) * mm});
            skLineSegment(sketch, "E640", {"start": v(-49.82, 52.71) * mm, "end": v(-49.99, 53.12) * mm});
            skLineSegment(sketch, "E641", {"start": v(-49.99, 53.12) * mm, "end": v(-50.29, 53.97) * mm});
            skLineSegment(sketch, "E642", {"start": v(-50.29, 53.97) * mm, "end": v(-50.43, 54.4) * mm});
            skLineSegment(sketch, "E643", {"start": v(-50.43, 54.4) * mm, "end": v(-49.55, 55.1) * mm});
            skLineSegment(sketch, "E644", {"start": v(-49.55, 55.1) * mm, "end": v(-49.16, 54.88) * mm});
            skLineSegment(sketch, "E645", {"start": v(-49.16, 54.88) * mm, "end": v(-48.4, 54.4) * mm});
            skLineSegment(sketch, "E646", {"start": v(-48.4, 54.4) * mm, "end": v(-48.03, 54.16) * mm});
            skLineSegment(sketch, "E647", {"start": v(-48.03, 54.16) * mm, "end": v(-47.12, 54.87) * mm});
            skLineSegment(sketch, "E648", {"start": v(-47.12, 54.87) * mm, "end": v(-47.26, 55.29) * mm});
            skLineSegment(sketch, "E649", {"start": v(-47.26, 55.29) * mm, "end": v(-47.52, 56.14) * mm});
            skLineSegment(sketch, "E650", {"start": v(-47.52, 56.14) * mm, "end": v(-47.64, 56.58) * mm});
            skLineSegment(sketch, "E651", {"start": v(-47.64, 56.58) * mm, "end": v(-46.73, 57.24) * mm});
            skLineSegment(sketch, "E652", {"start": v(-46.73, 57.24) * mm, "end": v(-46.35, 57) * mm});
            skLineSegment(sketch, "E653", {"start": v(-46.35, 57) * mm, "end": v(-45.62, 56.49) * mm});
            skLineSegment(sketch, "E654", {"start": v(-45.62, 56.49) * mm, "end": v(-45.26, 56.23) * mm});
            skLineSegment(sketch, "E655", {"start": v(-45.26, 56.23) * mm, "end": v(-44.31, 56.88) * mm});
            skLineSegment(sketch, "E656", {"start": v(-44.31, 56.88) * mm, "end": v(-44.43, 57.3) * mm});
            skLineSegment(sketch, "E657", {"start": v(-44.43, 57.3) * mm, "end": v(-44.65, 58.18) * mm});
            skLineSegment(sketch, "E658", {"start": v(-44.65, 58.18) * mm, "end": v(-44.74, 58.62) * mm});
            skLineSegment(sketch, "E659", {"start": v(-44.74, 58.62) * mm, "end": v(-43.8, 59.23) * mm});
            skLineSegment(sketch, "E660", {"start": v(-43.8, 59.23) * mm, "end": v(-43.44, 58.97) * mm});
            skLineSegment(sketch, "E661", {"start": v(-43.44, 58.97) * mm, "end": v(-42.73, 58.43) * mm});
            skLineSegment(sketch, "E662", {"start": v(-42.73, 58.43) * mm, "end": v(-42.38, 58.15) * mm});
            skLineSegment(sketch, "E663", {"start": v(-42.38, 58.15) * mm, "end": v(-41.4, 58.75) * mm});
            skLineSegment(sketch, "E664", {"start": v(-41.4, 58.75) * mm, "end": v(-41.5, 59.19) * mm});
            skLineSegment(sketch, "E665", {"start": v(-41.5, 59.19) * mm, "end": v(-41.67, 60.06) * mm});
            skLineSegment(sketch, "E666", {"start": v(-41.67, 60.06) * mm, "end": v(-41.75, 60.5) * mm});
            skLineSegment(sketch, "E667", {"start": v(-41.75, 60.5) * mm, "end": v(-40.78, 61.08) * mm});
            skLineSegment(sketch, "E668", {"start": v(-40.78, 61.08) * mm, "end": v(-40.43, 60.8) * mm});
            skLineSegment(sketch, "E669", {"start": v(-40.43, 60.8) * mm, "end": v(-39.75, 60.22) * mm});
            skLineSegment(sketch, "E670", {"start": v(-39.75, 60.22) * mm, "end": v(-39.42, 59.92) * mm});
            skLineSegment(sketch, "E671", {"start": v(-39.42, 59.92) * mm, "end": v(-38.4, 60.48) * mm});
            skLineSegment(sketch, "E672", {"start": v(-38.4, 60.48) * mm, "end": v(-38.48, 60.91) * mm});
            skLineSegment(sketch, "E673", {"start": v(-38.48, 60.91) * mm, "end": v(-38.61, 61.8) * mm});
            skLineSegment(sketch, "E674", {"start": v(-38.61, 61.8) * mm, "end": v(-38.66, 62.25) * mm});
            skLineSegment(sketch, "E675", {"start": v(-38.66, 62.25) * mm, "end": v(-37.66, 62.77) * mm});
            skLineSegment(sketch, "E676", {"start": v(-37.66, 62.77) * mm, "end": v(-37.33, 62.47) * mm});
            skLineSegment(sketch, "E677", {"start": v(-37.33, 62.47) * mm, "end": v(-36.68, 61.85) * mm});
            skLineSegment(sketch, "E678", {"start": v(-36.68, 61.85) * mm, "end": v(-36.36, 61.54) * mm});
            skLineSegment(sketch, "E679", {"start": v(-36.36, 61.54) * mm, "end": v(-35.33, 62.05) * mm});
            skLineSegment(sketch, "E680", {"start": v(-35.33, 62.05) * mm, "end": v(-35.38, 62.49) * mm});
            skLineSegment(sketch, "E681", {"start": v(-35.38, 62.49) * mm, "end": v(-35.46, 63.38) * mm});
            skLineSegment(sketch, "E682", {"start": v(-35.46, 63.38) * mm, "end": v(-35.5, 63.83) * mm});
            skLineSegment(sketch, "E683", {"start": v(-35.5, 63.83) * mm, "end": v(-34.47, 64.3) * mm});
            skLineSegment(sketch, "E684", {"start": v(-34.47, 64.3) * mm, "end": v(-34.15, 63.98) * mm});
            skLineSegment(sketch, "E685", {"start": v(-34.15, 63.98) * mm, "end": v(-33.53, 63.34) * mm});
            skLineSegment(sketch, "E686", {"start": v(-33.53, 63.34) * mm, "end": v(-33.23, 63) * mm});
            skLineSegment(sketch, "E687", {"start": v(-33.23, 63) * mm, "end": v(-32.17, 63.46) * mm});
            skLineSegment(sketch, "E688", {"start": v(-32.17, 63.46) * mm, "end": v(-32.2, 63.9) * mm});
            skLineSegment(sketch, "E689", {"start": v(-32.2, 63.9) * mm, "end": v(-32.24, 64.8) * mm});
            skLineSegment(sketch, "E690", {"start": v(-32.24, 64.8) * mm, "end": v(-32.25, 65.25) * mm});
            skLineSegment(sketch, "E691", {"start": v(-32.25, 65.25) * mm, "end": v(-31.2, 65.67) * mm});
            skLineSegment(sketch, "E692", {"start": v(-31.2, 65.67) * mm, "end": v(-30.9, 65.33) * mm});
            skLineSegment(sketch, "E693", {"start": v(-30.9, 65.33) * mm, "end": v(-30.31, 64.66) * mm});
            skLineSegment(sketch, "E694", {"start": v(-30.31, 64.66) * mm, "end": v(-30.03, 64.32) * mm});
            skLineSegment(sketch, "E695", {"start": v(-30.03, 64.32) * mm, "end": v(-28.95, 64.72) * mm});
            skLineSegment(sketch, "E696", {"start": v(-28.95, 64.72) * mm, "end": v(-28.96, 65.16) * mm});
            skLineSegment(sketch, "E697", {"start": v(-28.96, 65.16) * mm, "end": v(-28.95, 66.05) * mm});
            skLineSegment(sketch, "E698", {"start": v(-28.95, 66.05) * mm, "end": v(-28.94, 66.5) * mm});
            skLineSegment(sketch, "E699", {"start": v(-28.94, 66.5) * mm, "end": v(-27.87, 66.87) * mm});
            skLineSegment(sketch, "E700", {"start": v(-27.87, 66.87) * mm, "end": v(-27.58, 66.52) * mm});
            skLineSegment(sketch, "E701", {"start": v(-27.58, 66.52) * mm, "end": v(-27.03, 65.82) * mm});
            skLineSegment(sketch, "E702", {"start": v(-27.03, 65.82) * mm, "end": v(-26.77, 65.46) * mm});
            skLineSegment(sketch, "E703", {"start": v(-26.77, 65.46) * mm, "end": v(-25.67, 65.8) * mm});
            skLineSegment(sketch, "E704", {"start": v(-25.67, 65.8) * mm, "end": v(-25.66, 66.25) * mm});
            skLineSegment(sketch, "E705", {"start": v(-25.66, 66.25) * mm, "end": v(-25.6, 67.14) * mm});
            skLineSegment(sketch, "E706", {"start": v(-25.6, 67.14) * mm, "end": v(-25.57, 67.6) * mm});
            skLineSegment(sketch, "E707", {"start": v(-25.57, 67.6) * mm, "end": v(-24.48, 67.9) * mm});
            skLineSegment(sketch, "E708", {"start": v(-24.48, 67.9) * mm, "end": v(-24.21, 67.54) * mm});
            skLineSegment(sketch, "E709", {"start": v(-24.21, 67.54) * mm, "end": v(-23.7, 66.81) * mm});
            skLineSegment(sketch, "E710", {"start": v(-23.7, 66.81) * mm, "end": v(-23.45, 66.44) * mm});
            skLineSegment(sketch, "E711", {"start": v(-23.45, 66.44) * mm, "end": v(-22.34, 66.73) * mm});
            skLineSegment(sketch, "E712", {"start": v(-22.34, 66.73) * mm, "end": v(-22.3, 67.17) * mm});
            skLineSegment(sketch, "E713", {"start": v(-22.3, 67.17) * mm, "end": v(-22.2, 68.06) * mm});
            skLineSegment(sketch, "E714", {"start": v(-22.2, 68.06) * mm, "end": v(-22.15, 68.5) * mm});
            skLineSegment(sketch, "E715", {"start": v(-22.15, 68.5) * mm, "end": v(-21.05, 68.76) * mm});
            skLineSegment(sketch, "E716", {"start": v(-21.05, 68.76) * mm, "end": v(-20.8, 68.39) * mm});
            skLineSegment(sketch, "E717", {"start": v(-20.8, 68.39) * mm, "end": v(-20.32, 67.63) * mm});
            skLineSegment(sketch, "E718", {"start": v(-20.32, 67.63) * mm, "end": v(-20.1, 67.25) * mm});
            skLineSegment(sketch, "E719", {"start": v(-20.1, 67.25) * mm, "end": v(-18.96, 67.49) * mm});
            skLineSegment(sketch, "E720", {"start": v(-18.96, 67.49) * mm, "end": v(-18.9, 67.93) * mm});
            skLineSegment(sketch, "E721", {"start": v(-18.9, 67.93) * mm, "end": v(-18.77, 68.8) * mm});
            skLineSegment(sketch, "E722", {"start": v(-18.77, 68.8) * mm, "end": v(-18.68, 69.25) * mm});
            skLineSegment(sketch, "E723", {"start": v(-18.68, 69.25) * mm, "end": v(-17.58, 69.45) * mm});
            skLineSegment(sketch, "E724", {"start": v(-17.58, 69.45) * mm, "end": v(-17.34, 69.07) * mm});
            skLineSegment(sketch, "E725", {"start": v(-17.34, 69.07) * mm, "end": v(-16.9, 68.29) * mm});
            skLineSegment(sketch, "E726", {"start": v(-16.9, 68.29) * mm, "end": v(-16.7, 67.9) * mm});
            skLineSegment(sketch, "E727", {"start": v(-16.7, 67.9) * mm, "end": v(-15.56, 68.07) * mm});
            skLineSegment(sketch, "E728", {"start": v(-15.56, 68.07) * mm, "end": v(-15.48, 68.5) * mm});
            skLineSegment(sketch, "E729", {"start": v(-15.48, 68.5) * mm, "end": v(-15.3, 69.38) * mm});
            skLineSegment(sketch, "E730", {"start": v(-15.3, 69.38) * mm, "end": v(-15.19, 69.82) * mm});
            skLineSegment(sketch, "E731", {"start": v(-15.19, 69.82) * mm, "end": v(-14.07, 69.96) * mm});
            skLineSegment(sketch, "E732", {"start": v(-14.07, 69.96) * mm, "end": v(-13.86, 69.57) * mm});
            skLineSegment(sketch, "E733", {"start": v(-13.86, 69.57) * mm, "end": v(-13.46, 68.77) * mm});
            skLineSegment(sketch, "E734", {"start": v(-13.46, 68.77) * mm, "end": v(-13.27, 68.37) * mm});
            skLineSegment(sketch, "E735", {"start": v(-13.27, 68.37) * mm, "end": v(-12.12, 68.49) * mm});
            skLineSegment(sketch, "E736", {"start": v(-12.12, 68.49) * mm, "end": v(-12.02, 68.92) * mm});
            skLineSegment(sketch, "E737", {"start": v(-12.02, 68.92) * mm, "end": v(-11.8, 69.78) * mm});
            skLineSegment(sketch, "E738", {"start": v(-11.8, 69.78) * mm, "end": v(-11.67, 70.21) * mm});
            skLineSegment(sketch, "E739", {"start": v(-11.67, 70.21) * mm, "end": v(-10.54, 70.3) * mm});
            skLineSegment(sketch, "E740", {"start": v(-10.54, 70.3) * mm, "end": v(-10.35, 69.9) * mm});
            skLineSegment(sketch, "E741", {"start": v(-10.35, 69.9) * mm, "end": v(-10, 69.08) * mm});
            skLineSegment(sketch, "E742", {"start": v(-10, 69.08) * mm, "end": v(-9.83, 68.67) * mm});
            skLineSegment(sketch, "E743", {"start": v(-9.83, 68.67) * mm, "end": v(-8.67, 68.73) * mm});
            skLineSegment(sketch, "E744", {"start": v(-8.67, 68.73) * mm, "end": v(-8.55, 69.15) * mm});
            skLineSegment(sketch, "E745", {"start": v(-8.55, 69.15) * mm, "end": v(-8.28, 70) * mm});
            skLineSegment(sketch, "E746", {"start": v(-8.28, 70) * mm, "end": v(-8.13, 70.43) * mm});
            skLineSegment(sketch, "E747", {"start": v(-8.13, 70.43) * mm, "end": v(-7, 70.46) * mm});
            skLineSegment(sketch, "E748", {"start": v(-7, 70.46) * mm, "end": v(-6.83, 70.04) * mm});
            skLineSegment(sketch, "E749", {"start": v(-6.83, 70.04) * mm, "end": v(-6.52, 69.2) * mm});
            skLineSegment(sketch, "E750", {"start": v(-6.52, 69.2) * mm, "end": v(-6.37, 68.79) * mm});
            skLineSegment(sketch, "E751", {"start": v(-6.37, 68.79) * mm, "end": v(-5.22, 68.8) * mm});
            skLineSegment(sketch, "E752", {"start": v(-5.22, 68.8) * mm, "end": v(-5.07, 69.21) * mm});
            skLineSegment(sketch, "E753", {"start": v(-5.07, 69.21) * mm, "end": v(-4.76, 70.05) * mm});
            skLineSegment(sketch, "E754", {"start": v(-4.76, 70.05) * mm, "end": v(-4.59, 70.47) * mm});
            skLineSegment(sketch, "E755", {"start": v(-4.59, 70.47) * mm, "end": v(-3.46, 70.44) * mm});
            skLineSegment(sketch, "E756", {"start": v(-3.46, 70.44) * mm, "end": v(-3.31, 70.02) * mm});
            skLineSegment(sketch, "E757", {"start": v(-3.31, 70.02) * mm, "end": v(-3.04, 69.17) * mm});
            skLineSegment(sketch, "E758", {"start": v(-3.04, 69.17) * mm, "end": v(-2.91, 68.74) * mm});
            skLineSegment(sketch, "E759", {"start": v(-2.91, 68.74) * mm, "end": v(-1.76, 68.69) * mm});
            skLineSegment(sketch, "E760", {"start": v(-1.76, 68.69) * mm, "end": v(-1.6, 69.1) * mm});
            skLineSegment(sketch, "E761", {"start": v(-1.6, 69.1) * mm, "end": v(-1.24, 69.92) * mm});
            skLineSegment(sketch, "E762", {"start": v(-1.24, 69.92) * mm, "end": v(-1.05, 70.32) * mm});
            skLineSegment(sketch, "E763", {"start": v(-1.05, 70.32) * mm, "end": v(0.07, 70.24) * mm});
            skLineSegment(sketch, "E764", {"start": v(0.07, 70.24) * mm, "end": v(0.2, 69.81) * mm});
            skLineSegment(sketch, "E765", {"start": v(0.2, 69.81) * mm, "end": v(0.43, 68.95) * mm});
            skLineSegment(sketch, "E766", {"start": v(0.43, 68.95) * mm, "end": v(0.54, 68.52) * mm});
            skLineSegment(sketch, "E767", {"start": v(0.54, 68.52) * mm, "end": v(1.68, 68.4) * mm});
            skLineSegment(sketch, "E768", {"start": v(1.68, 68.4) * mm, "end": v(1.87, 68.8) * mm});
            skLineSegment(sketch, "E769", {"start": v(1.87, 68.8) * mm, "end": v(2.27, 69.6) * mm});
            skLineSegment(sketch, "E770", {"start": v(2.27, 69.6) * mm, "end": v(2.48, 70) * mm});
            skLineSegment(sketch, "E771", {"start": v(2.48, 70) * mm, "end": v(3.6, 69.87) * mm});
            skLineSegment(sketch, "E772", {"start": v(3.6, 69.87) * mm, "end": v(3.7, 69.43) * mm});
            skLineSegment(sketch, "E773", {"start": v(3.7, 69.43) * mm, "end": v(3.9, 68.56) * mm});
            skLineSegment(sketch, "E774", {"start": v(3.9, 68.56) * mm, "end": v(3.97, 68.12) * mm});
            skLineSegment(sketch, "E775", {"start": v(3.97, 68.12) * mm, "end": v(5.11, 67.95) * mm});
            skLineSegment(sketch, "E776", {"start": v(5.11, 67.95) * mm, "end": v(5.32, 68.34) * mm});
            skLineSegment(sketch, "E777", {"start": v(5.32, 68.34) * mm, "end": v(5.75, 69.12) * mm});
            skLineSegment(sketch, "E778", {"start": v(5.75, 69.12) * mm, "end": v(5.98, 69.51) * mm});
            skLineSegment(sketch, "E779", {"start": v(5.98, 69.51) * mm, "end": v(7.1, 69.32) * mm});
            skLineSegment(sketch, "E780", {"start": v(7.1, 69.32) * mm, "end": v(7.18, 68.87) * mm});
            skLineSegment(sketch, "E781", {"start": v(7.18, 68.87) * mm, "end": v(7.32, 68) * mm});
            skLineSegment(sketch, "E782", {"start": v(7.32, 68) * mm, "end": v(7.38, 67.55) * mm});
            skLineSegment(sketch, "E783", {"start": v(7.38, 67.55) * mm, "end": v(8.51, 67.33) * mm});
            skLineSegment(sketch, "E784", {"start": v(8.51, 67.33) * mm, "end": v(8.74, 67.7) * mm});
            skLineSegment(sketch, "E785", {"start": v(8.74, 67.7) * mm, "end": v(9.21, 68.46) * mm});
            skLineSegment(sketch, "E786", {"start": v(9.21, 68.46) * mm, "end": v(9.46, 68.84) * mm});
            skLineSegment(sketch, "E787", {"start": v(9.46, 68.84) * mm, "end": v(10.56, 68.6) * mm});
            skLineSegment(sketch, "E788", {"start": v(10.56, 68.6) * mm, "end": v(10.62, 68.14) * mm});
            skLineSegment(sketch, "E789", {"start": v(10.62, 68.14) * mm, "end": v(10.72, 67.26) * mm});
            skLineSegment(sketch, "E790", {"start": v(10.72, 67.26) * mm, "end": v(10.76, 66.82) * mm});
            skLineSegment(sketch, "E791", {"start": v(10.76, 66.82) * mm, "end": v(11.88, 66.53) * mm});
            skLineSegment(sketch, "E792", {"start": v(11.88, 66.53) * mm, "end": v(12.12, 66.9) * mm});
            skLineSegment(sketch, "E793", {"start": v(12.12, 66.9) * mm, "end": v(12.63, 67.63) * mm});
            skLineSegment(sketch, "E794", {"start": v(12.63, 67.63) * mm, "end": v(12.9, 68) * mm});
            skLineSegment(sketch, "E795", {"start": v(12.9, 68) * mm, "end": v(13.98, 67.7) * mm});
            skLineSegment(sketch, "E796", {"start": v(13.98, 67.7) * mm, "end": v(14.02, 67.24) * mm});
            skLineSegment(sketch, "E797", {"start": v(14.02, 67.24) * mm, "end": v(14.08, 66.35) * mm});
            skLineSegment(sketch, "E798", {"start": v(14.08, 66.35) * mm, "end": v(14.1, 65.9) * mm});
            skLineSegment(sketch, "E799", {"start": v(14.1, 65.9) * mm, "end": v(15.2, 65.57) * mm});
            skLineSegment(sketch, "E800", {"start": v(15.2, 65.57) * mm, "end": v(15.46, 65.93) * mm});
            skLineSegment(sketch, "E801", {"start": v(15.46, 65.93) * mm, "end": v(16, 66.63) * mm});
            skLineSegment(sketch, "E802", {"start": v(16, 66.63) * mm, "end": v(16.3, 66.98) * mm});
            skLineSegment(sketch, "E803", {"start": v(16.3, 66.98) * mm, "end": v(17.36, 66.62) * mm});
            skLineSegment(sketch, "E804", {"start": v(17.36, 66.62) * mm, "end": v(17.38, 66.17) * mm});
            skLineSegment(sketch, "E805", {"start": v(17.38, 66.17) * mm, "end": v(17.39, 65.28) * mm});
            skLineSegment(sketch, "E806", {"start": v(17.39, 65.28) * mm, "end": v(17.38, 64.83) * mm});
            skLineSegment(sketch, "E807", {"start": v(17.38, 64.83) * mm, "end": v(18.47, 64.44) * mm});
            skLineSegment(sketch, "E808", {"start": v(18.47, 64.44) * mm, "end": v(18.74, 64.78) * mm});
            skLineSegment(sketch, "E809", {"start": v(18.74, 64.78) * mm, "end": v(19.33, 65.46) * mm});
            skLineSegment(sketch, "E810", {"start": v(19.33, 65.46) * mm, "end": v(19.63, 65.8) * mm});
            skLineSegment(sketch, "E811", {"start": v(19.63, 65.8) * mm, "end": v(20.68, 65.38) * mm});
            skLineSegment(sketch, "E812", {"start": v(20.68, 65.38) * mm, "end": v(20.67, 64.93) * mm});
            skLineSegment(sketch, "E813", {"start": v(20.67, 64.93) * mm, "end": v(20.64, 64.04) * mm});
            skLineSegment(sketch, "E814", {"start": v(20.64, 64.04) * mm, "end": v(20.61, 63.6) * mm});
            skLineSegment(sketch, "E815", {"start": v(20.61, 63.6) * mm, "end": v(21.67, 63.15) * mm});
            skLineSegment(sketch, "E816", {"start": v(21.67, 63.15) * mm, "end": v(21.97, 63.48) * mm});
            skLineSegment(sketch, "E817", {"start": v(21.97, 63.48) * mm, "end": v(22.59, 64.12) * mm});
            skLineSegment(sketch, "E818", {"start": v(22.59, 64.12) * mm, "end": v(22.9, 64.44) * mm});
            skLineSegment(sketch, "E819", {"start": v(22.9, 64.44) * mm, "end": v(23.93, 63.98) * mm});
            skLineSegment(sketch, "E820", {"start": v(23.93, 63.98) * mm, "end": v(23.9, 63.53) * mm});
            skLineSegment(sketch, "E821", {"start": v(23.9, 63.53) * mm, "end": v(23.82, 62.64) * mm});
            skLineSegment(sketch, "E822", {"start": v(23.82, 62.64) * mm, "end": v(23.77, 62.2) * mm});
            skLineSegment(sketch, "E823", {"start": v(23.77, 62.2) * mm, "end": v(24.81, 61.7) * mm});
            skLineSegment(sketch, "E824", {"start": v(24.81, 61.7) * mm, "end": v(25.12, 62.01) * mm});
            skLineSegment(sketch, "E825", {"start": v(25.12, 62.01) * mm, "end": v(25.77, 62.63) * mm});
            skLineSegment(sketch, "E826", {"start": v(25.77, 62.63) * mm, "end": v(26.1, 62.93) * mm});
            skLineSegment(sketch, "E827", {"start": v(26.1, 62.93) * mm, "end": v(27.1, 62.41) * mm});
            skLineSegment(sketch, "E828", {"start": v(27.1, 62.41) * mm, "end": v(27.06, 61.96) * mm});
            skLineSegment(sketch, "E829", {"start": v(27.06, 61.96) * mm, "end": v(26.93, 61.08) * mm});
            skLineSegment(sketch, "E830", {"start": v(26.93, 61.08) * mm, "end": v(26.86, 60.64) * mm});
            skLineSegment(sketch, "E831", {"start": v(26.86, 60.64) * mm, "end": v(27.87, 60.09) * mm});
            skLineSegment(sketch, "E832", {"start": v(27.87, 60.09) * mm, "end": v(28.2, 60.39) * mm});
            skLineSegment(sketch, "E833", {"start": v(28.2, 60.39) * mm, "end": v(28.88, 60.97) * mm});
            skLineSegment(sketch, "E834", {"start": v(28.88, 60.97) * mm, "end": v(29.23, 61.25) * mm});
            skLineSegment(sketch, "E835", {"start": v(29.23, 61.25) * mm, "end": v(30.2, 60.69) * mm});
            skLineSegment(sketch, "E836", {"start": v(30.2, 60.69) * mm, "end": v(30.13, 60.24) * mm});
            skLineSegment(sketch, "E837", {"start": v(30.13, 60.24) * mm, "end": v(29.96, 59.37) * mm});
            skLineSegment(sketch, "E838", {"start": v(29.96, 59.37) * mm, "end": v(29.87, 58.93) * mm});
            skLineSegment(sketch, "E839", {"start": v(29.87, 58.93) * mm, "end": v(30.85, 58.33) * mm});
            skLineSegment(sketch, "E840", {"start": v(30.85, 58.33) * mm, "end": v(31.2, 58.61) * mm});
            skLineSegment(sketch, "E841", {"start": v(31.2, 58.61) * mm, "end": v(31.9, 59.16) * mm});
            skLineSegment(sketch, "E842", {"start": v(31.9, 59.16) * mm, "end": v(32.26, 59.42) * mm});
            skLineSegment(sketch, "E843", {"start": v(32.26, 59.42) * mm, "end": v(33.2, 58.81) * mm});
            skLineSegment(sketch, "E844", {"start": v(33.2, 58.81) * mm, "end": v(33.11, 58.37) * mm});
            skLineSegment(sketch, "E845", {"start": v(33.11, 58.37) * mm, "end": v(32.9, 57.5) * mm});
            skLineSegment(sketch, "E846", {"start": v(32.9, 57.5) * mm, "end": v(32.78, 57.08) * mm});
            skLineSegment(sketch, "E847", {"start": v(32.78, 57.08) * mm, "end": v(33.73, 56.42) * mm});
            skLineSegment(sketch, "E848", {"start": v(33.73, 56.42) * mm, "end": v(34.09, 56.69) * mm});
            skLineSegment(sketch, "E849", {"start": v(34.09, 56.69) * mm, "end": v(34.82, 57.2) * mm});
            skLineSegment(sketch, "E850", {"start": v(34.82, 57.2) * mm, "end": v(35.2, 57.45) * mm});
            skLineSegment(sketch, "E851", {"start": v(35.2, 57.45) * mm, "end": v(36.11, 56.79) * mm});
            skLineSegment(sketch, "E852", {"start": v(36.11, 56.79) * mm, "end": v(36, 56.35) * mm});
            skLineSegment(sketch, "E853", {"start": v(36, 56.35) * mm, "end": v(35.74, 55.5) * mm});
            skLineSegment(sketch, "E854", {"start": v(35.74, 55.5) * mm, "end": v(35.6, 55.07) * mm});
            skLineSegment(sketch, "E855", {"start": v(35.6, 55.07) * mm, "end": v(36.52, 54.38) * mm});
            skLineSegment(sketch, "E856", {"start": v(36.52, 54.38) * mm, "end": v(36.89, 54.62) * mm});
            skLineSegment(sketch, "E857", {"start": v(36.89, 54.62) * mm, "end": v(37.65, 55.1) * mm});
            skLineSegment(sketch, "E858", {"start": v(37.65, 55.1) * mm, "end": v(38.03, 55.32) * mm});
            skLineSegment(sketch, "E859", {"start": v(38.03, 55.32) * mm, "end": v(38.91, 54.62) * mm});
            skLineSegment(sketch, "E860", {"start": v(38.91, 54.62) * mm, "end": v(38.77, 54.19) * mm});
            skLineSegment(sketch, "E861", {"start": v(38.77, 54.19) * mm, "end": v(38.48, 53.35) * mm});
            skLineSegment(sketch, "E862", {"start": v(38.48, 53.35) * mm, "end": v(38.32, 52.93) * mm});
            skLineSegment(sketch, "E863", {"start": v(38.32, 52.93) * mm, "end": v(39.2, 52.19) * mm});
            skLineSegment(sketch, "E864", {"start": v(39.2, 52.19) * mm, "end": v(39.58, 52.42) * mm});
            skLineSegment(sketch, "E865", {"start": v(39.58, 52.42) * mm, "end": v(40.36, 52.85) * mm});
            skLineSegment(sketch, "E866", {"start": v(40.36, 52.85) * mm, "end": v(40.76, 53.06) * mm});
            skLineSegment(sketch, "E867", {"start": v(40.76, 53.06) * mm, "end": v(41.6, 52.31) * mm});
            skLineSegment(sketch, "E868", {"start": v(41.6, 52.31) * mm, "end": v(41.44, 51.9) * mm});
            skLineSegment(sketch, "E869", {"start": v(41.44, 51.9) * mm, "end": v(41.1, 51.06) * mm});
            skLineSegment(sketch, "E870", {"start": v(41.1, 51.06) * mm, "end": v(40.92, 50.66) * mm});
            skLineSegment(sketch, "E871", {"start": v(40.92, 50.66) * mm, "end": v(41.76, 49.87) * mm});
            skLineSegment(sketch, "E872", {"start": v(41.76, 49.87) * mm, "end": v(42.15, 50.08) * mm});
            skLineSegment(sketch, "E873", {"start": v(42.15, 50.08) * mm, "end": v(42.96, 50.47) * mm});
            skLineSegment(sketch, "E874", {"start": v(42.96, 50.47) * mm, "end": v(43.37, 50.66) * mm});
            skLineSegment(sketch, "E875", {"start": v(43.37, 50.66) * mm, "end": v(44.17, 49.87) * mm});
            skLineSegment(sketch, "E876", {"start": v(44.17, 49.87) * mm, "end": v(43.99, 49.46) * mm});
            skLineSegment(sketch, "E877", {"start": v(43.99, 49.46) * mm, "end": v(43.6, 48.65) * mm});
            skLineSegment(sketch, "E878", {"start": v(43.6, 48.65) * mm, "end": v(43.4, 48.26) * mm});
            skLineSegment(sketch, "E879", {"start": v(43.4, 48.26) * mm, "end": v(44.2, 47.43) * mm});
            skLineSegment(sketch, "E880", {"start": v(44.2, 47.43) * mm, "end": v(44.61, 47.62) * mm});
            skLineSegment(sketch, "E881", {"start": v(44.61, 47.62) * mm, "end": v(45.43, 47.97) * mm});
            skLineSegment(sketch, "E882", {"start": v(45.43, 47.97) * mm, "end": v(45.85, 48.14) * mm});
            skLineSegment(sketch, "E883", {"start": v(45.85, 48.14) * mm, "end": v(46.61, 47.3) * mm});
            skLineSegment(sketch, "E884", {"start": v(46.61, 47.3) * mm, "end": v(46.4, 46.9) * mm});
            skLineSegment(sketch, "E885", {"start": v(46.4, 46.9) * mm, "end": v(45.99, 46.12) * mm});
            skLineSegment(sketch, "E886", {"start": v(45.99, 46.12) * mm, "end": v(45.77, 45.73) * mm});
            skLineSegment(sketch, "E887", {"start": v(45.77, 45.73) * mm, "end": v(46.53, 44.86) * mm});
            skLineSegment(sketch, "E888", {"start": v(46.53, 44.86) * mm, "end": v(46.94, 45.03) * mm});
            skLineSegment(sketch, "E889", {"start": v(46.94, 45.03) * mm, "end": v(47.78, 45.34) * mm});
            skLineSegment(sketch, "E890", {"start": v(47.78, 45.34) * mm, "end": v(48.2, 45.5) * mm});
            skLineSegment(sketch, "E891", {"start": v(48.2, 45.5) * mm, "end": v(48.92, 44.62) * mm});
            skLineSegment(sketch, "E892", {"start": v(48.92, 44.62) * mm, "end": v(48.7, 44.23) * mm});
            skLineSegment(sketch, "E893", {"start": v(48.7, 44.23) * mm, "end": v(48.24, 43.47) * mm});
            skLineSegment(sketch, "E894", {"start": v(48.24, 43.47) * mm, "end": v(48, 43.1) * mm});
            skLineSegment(sketch, "E895", {"start": v(48, 43.1) * mm, "end": v(48.72, 42.19) * mm});
            skLineSegment(sketch, "E896", {"start": v(48.72, 42.19) * mm, "end": v(49.13, 42.33) * mm});
            skLineSegment(sketch, "E897", {"start": v(49.13, 42.33) * mm, "end": v(49.99, 42.6) * mm});
            skLineSegment(sketch, "E898", {"start": v(49.99, 42.6) * mm, "end": v(50.42, 42.73) * mm});
            skLineSegment(sketch, "E899", {"start": v(50.42, 42.73) * mm, "end": v(51.1, 41.83) * mm});
            skLineSegment(sketch, "E900", {"start": v(51.1, 41.83) * mm, "end": v(50.85, 41.45) * mm});
            skLineSegment(sketch, "E901", {"start": v(50.85, 41.45) * mm, "end": v(50.36, 40.7) * mm});
            skLineSegment(sketch, "E902", {"start": v(50.36, 40.7) * mm, "end": v(50.1, 40.34) * mm});
            skLineSegment(sketch, "E903", {"start": v(50.1, 40.34) * mm, "end": v(50.77, 39.4) * mm});
            skLineSegment(sketch, "E904", {"start": v(50.77, 39.4) * mm, "end": v(51.2, 39.53) * mm});
            skLineSegment(sketch, "E905", {"start": v(51.2, 39.53) * mm, "end": v(52.06, 39.76) * mm});
            skLineSegment(sketch, "E906", {"start": v(52.06, 39.76) * mm, "end": v(52.5, 39.86) * mm});
            skLineSegment(sketch, "E907", {"start": v(52.5, 39.86) * mm, "end": v(53.12, 38.93) * mm});
            skLineSegment(sketch, "E908", {"start": v(53.12, 38.93) * mm, "end": v(52.87, 38.56) * mm});
            skLineSegment(sketch, "E909", {"start": v(52.87, 38.56) * mm, "end": v(52.33, 37.84) * mm});
            skLineSegment(sketch, "E910", {"start": v(52.33, 37.84) * mm, "end": v(52.06, 37.5) * mm});
            skLineSegment(sketch, "E911", {"start": v(52.06, 37.5) * mm, "end": v(52.68, 36.52) * mm});
            skLineSegment(sketch, "E912", {"start": v(52.68, 36.52) * mm, "end": v(53.1, 36.62) * mm});
            skLineSegment(sketch, "E913", {"start": v(53.1, 36.62) * mm, "end": v(53.98, 36.8) * mm});
            skLineSegment(sketch, "E914", {"start": v(53.98, 36.8) * mm, "end": v(54.42, 36.89) * mm});
            skLineSegment(sketch, "E915", {"start": v(54.42, 36.89) * mm, "end": v(55, 35.92) * mm});
            skLineSegment(sketch, "E916", {"start": v(55, 35.92) * mm, "end": v(54.73, 35.57) * mm});
            skLineSegment(sketch, "E917", {"start": v(54.73, 35.57) * mm, "end": v(54.16, 34.88) * mm});
            skLineSegment(sketch, "E918", {"start": v(54.16, 34.88) * mm, "end": v(53.87, 34.55) * mm});
            skLineSegment(sketch, "E919", {"start": v(53.87, 34.55) * mm, "end": v(54.44, 33.55) * mm});
            skLineSegment(sketch, "E920", {"start": v(54.44, 33.55) * mm, "end": v(54.87, 33.63) * mm});
            skLineSegment(sketch, "E921", {"start": v(54.87, 33.63) * mm, "end": v(55.76, 33.77) * mm});
            skLineSegment(sketch, "E922", {"start": v(55.76, 33.77) * mm, "end": v(56.2, 33.82) * mm});
            skLineSegment(sketch, "E923", {"start": v(56.2, 33.82) * mm, "end": v(56.73, 32.83) * mm});
            skLineSegment(sketch, "E924", {"start": v(56.73, 32.83) * mm, "end": v(56.44, 32.5) * mm});
            skLineSegment(sketch, "E925", {"start": v(56.44, 32.5) * mm, "end": v(55.84, 31.83) * mm});
            skLineSegment(sketch, "E926", {"start": v(55.84, 31.83) * mm, "end": v(55.53, 31.52) * mm});
            skLineSegment(sketch, "E927", {"start": v(55.53, 31.52) * mm, "end": v(56.05, 30.49) * mm});
            skLineSegment(sketch, "E928", {"start": v(56.05, 30.49) * mm, "end": v(56.49, 30.55) * mm});
            skLineSegment(sketch, "E929", {"start": v(56.49, 30.55) * mm, "end": v(57.37, 30.64) * mm});
            skLineSegment(sketch, "E930", {"start": v(57.37, 30.64) * mm, "end": v(57.82, 30.68) * mm});
            skLineSegment(sketch, "E931", {"start": v(57.82, 30.68) * mm, "end": v(58.3, 29.66) * mm});
            skLineSegment(sketch, "E932", {"start": v(58.3, 29.66) * mm, "end": v(58, 29.33) * mm});
            skLineSegment(sketch, "E933", {"start": v(58, 29.33) * mm, "end": v(57.36, 28.7) * mm});
            skLineSegment(sketch, "E934", {"start": v(57.36, 28.7) * mm, "end": v(57.03, 28.4) * mm});
            skLineSegment(sketch, "E935", {"start": v(57.03, 28.4) * mm, "end": v(57.5, 27.35) * mm});
            skLineSegment(sketch, "E936", {"start": v(57.5, 27.35) * mm, "end": v(57.94, 27.39) * mm});
            skLineSegment(sketch, "E937", {"start": v(57.94, 27.39) * mm, "end": v(58.83, 27.44) * mm});
            skLineSegment(sketch, "E938", {"start": v(58.83, 27.44) * mm, "end": v(59.28, 27.45) * mm});
            skLineSegment(sketch, "E939", {"start": v(59.28, 27.45) * mm, "end": v(59.71, 26.4) * mm});
            skLineSegment(sketch, "E940", {"start": v(59.71, 26.4) * mm, "end": v(59.39, 26.1) * mm});
            skLineSegment(sketch, "E941", {"start": v(59.39, 26.1) * mm, "end": v(58.72, 25.5) * mm});
            skLineSegment(sketch, "E942", {"start": v(58.72, 25.5) * mm, "end": v(58.38, 25.22) * mm});
            skLineSegment(sketch, "E943", {"start": v(58.38, 25.22) * mm, "end": v(58.8, 24.14) * mm});
            skLineSegment(sketch, "E944", {"start": v(58.8, 24.14) * mm, "end": v(59.24, 24.16) * mm});
            skLineSegment(sketch, "E945", {"start": v(59.24, 24.16) * mm, "end": v(60.13, 24.16) * mm});
            skLineSegment(sketch, "E946", {"start": v(60.13, 24.16) * mm, "end": v(60.58, 24.15) * mm});
            skLineSegment(sketch, "E947", {"start": v(60.58, 24.15) * mm, "end": v(60.96, 23.1) * mm});
            skLineSegment(sketch, "E948", {"start": v(60.96, 23.1) * mm, "end": v(60.62, 22.8) * mm});
            skLineSegment(sketch, "E949", {"start": v(60.62, 22.8) * mm, "end": v(59.92, 22.24) * mm});
            skLineSegment(sketch, "E950", {"start": v(59.92, 22.24) * mm, "end": v(59.57, 21.97) * mm});
            skLineSegment(sketch, "E951", {"start": v(59.57, 21.97) * mm, "end": v(59.93, 20.88) * mm});
            skLineSegment(sketch, "E952", {"start": v(59.93, 20.88) * mm, "end": v(60.37, 20.87) * mm});
            skLineSegment(sketch, "E953", {"start": v(60.37, 20.87) * mm, "end": v(61.26, 20.83) * mm});
            skLineSegment(sketch, "E954", {"start": v(61.26, 20.83) * mm, "end": v(61.71, 20.8) * mm});
            skLineSegment(sketch, "E955", {"start": v(61.71, 20.8) * mm, "end": v(62.03, 19.72) * mm});
            skLineSegment(sketch, "E956", {"start": v(62.03, 19.72) * mm, "end": v(61.68, 19.44) * mm});
            skLineSegment(sketch, "E957", {"start": v(61.68, 19.44) * mm, "end": v(60.95, 18.92) * mm});
            skLineSegment(sketch, "E958", {"start": v(60.95, 18.92) * mm, "end": v(60.59, 18.67) * mm});
            skLineSegment(sketch, "E959", {"start": v(60.59, 18.67) * mm, "end": v(60.9, 17.56) * mm});
            skLineSegment(sketch, "E960", {"start": v(60.9, 17.56) * mm, "end": v(61.33, 17.53) * mm});
            skLineSegment(sketch, "E961", {"start": v(61.33, 17.53) * mm, "end": v(62.22, 17.44) * mm});
            skLineSegment(sketch, "E962", {"start": v(62.22, 17.44) * mm, "end": v(62.67, 17.39) * mm});
            skLineSegment(sketch, "E963", {"start": v(62.67, 17.39) * mm, "end": v(62.94, 16.3) * mm});
            skLineSegment(sketch, "E964", {"start": v(62.94, 16.3) * mm, "end": v(62.57, 16.04) * mm});
            skLineSegment(sketch, "E965", {"start": v(62.57, 16.04) * mm, "end": v(61.82, 15.55) * mm});
            skLineSegment(sketch, "E966", {"start": v(61.82, 15.55) * mm, "end": v(61.44, 15.32) * mm});
            skLineSegment(sketch, "E967", {"start": v(61.44, 15.32) * mm, "end": v(61.7, 14.2) * mm});
            skLineSegment(sketch, "E968", {"start": v(61.7, 14.2) * mm, "end": v(62.13, 14.14) * mm});
            skLineSegment(sketch, "E969", {"start": v(62.13, 14.14) * mm, "end": v(63.01, 14.01) * mm});
            skLineSegment(sketch, "E970", {"start": v(63.01, 14.01) * mm, "end": v(63.46, 13.93) * mm});
            skLineSegment(sketch, "E971", {"start": v(63.46, 13.93) * mm, "end": v(63.67, 12.83) * mm});
            skLineSegment(sketch, "E972", {"start": v(63.67, 12.83) * mm, "end": v(63.29, 12.6) * mm});
            skLineSegment(sketch, "E973", {"start": v(63.29, 12.6) * mm, "end": v(62.52, 12.14) * mm});
            skLineSegment(sketch, "E974", {"start": v(62.52, 12.14) * mm, "end": v(62.13, 11.93) * mm});
            skLineSegment(sketch, "E975", {"start": v(62.13, 11.93) * mm, "end": v(62.32, 10.8) * mm});
            skLineSegment(sketch, "E976", {"start": v(62.32, 10.8) * mm, "end": v(62.75, 10.72) * mm});
            skLineSegment(sketch, "E977", {"start": v(62.75, 10.72) * mm, "end": v(63.63, 10.55) * mm});
            skLineSegment(sketch, "E978", {"start": v(63.63, 10.55) * mm, "end": v(64.07, 10.45) * mm});
            skLineSegment(sketch, "E979", {"start": v(64.07, 10.45) * mm, "end": v(64.23, 9.33) * mm});
            skLineSegment(sketch, "E980", {"start": v(64.23, 9.33) * mm, "end": v(63.83, 9.11) * mm});
            skLineSegment(sketch, "E981", {"start": v(63.83, 9.11) * mm, "end": v(63.04, 8.7) * mm});
            skLineSegment(sketch, "E982", {"start": v(63.04, 8.7) * mm, "end": v(62.64, 8.51) * mm});
            skLineSegment(sketch, "E983", {"start": v(62.64, 8.51) * mm, "end": v(62.77, 7.37) * mm});
            skLineSegment(sketch, "E984", {"start": v(62.77, 7.37) * mm, "end": v(63.2, 7.27) * mm});
            skLineSegment(sketch, "E985", {"start": v(63.2, 7.27) * mm, "end": v(64.07, 7.05) * mm});
            skLineSegment(sketch, "E986", {"start": v(64.07, 7.05) * mm, "end": v(64.5, 6.93) * mm});
            skLineSegment(sketch, "E987", {"start": v(64.5, 6.93) * mm, "end": v(64.6, 5.8) * mm});
            skLineSegment(sketch, "E988", {"start": v(64.6, 5.8) * mm, "end": v(64.2, 5.61) * mm});
            skLineSegment(sketch, "E989", {"start": v(64.2, 5.61) * mm, "end": v(63.4, 5.24) * mm});
            skLineSegment(sketch, "E990", {"start": v(63.4, 5.24) * mm, "end": v(62.98, 5.07) * mm});
            skLineSegment(sketch, "E991", {"start": v(62.98, 5.07) * mm, "end": v(63.06, 3.92) * mm});
            skLineSegment(sketch, "E992", {"start": v(63.06, 3.92) * mm, "end": v(63.49, 3.8) * mm});
            skLineSegment(sketch, "E993", {"start": v(63.49, 3.8) * mm, "end": v(64.34, 3.54) * mm});
            skLineSegment(sketch, "E994", {"start": v(64.34, 3.54) * mm, "end": v(64.77, 3.4) * mm});
            skLineSegment(sketch, "E995", {"start": v(64.77, 3.4) * mm, "end": v(64.81, 2.27) * mm});
            skLineSegment(sketch, "E996", {"start": v(64.81, 2.27) * mm, "end": v(64.4, 2.1) * mm});
            skLineSegment(sketch, "E997", {"start": v(64.4, 2.1) * mm, "end": v(63.57, 1.77) * mm});
            skLineSegment(sketch, "E998", {"start": v(63.57, 1.77) * mm, "end": v(63.15, 1.62) * mm});
            skLineSegment(sketch, "E999", {"start": v(63.15, 1.62) * mm, "end": v(63.17, 0.46) * mm});
            skLineSegment(sketch, "E1000", {"start": v(9.63, 4.08) * mm, "end": v(54.6, 3.63) * mm});
            skLineSegment(sketch, "E1001", {"start": v(54.6, 3.63) * mm, "end": v(56.57, 5.72) * mm});
            skLineSegment(sketch, "E1002", {"start": v(56.57, 5.72) * mm, "end": v(56, 10.08) * mm});
            skLineSegment(sketch, "E1003", {"start": v(56, 10.08) * mm, "end": v(55.15, 14.38) * mm});
            skLineSegment(sketch, "E1004", {"start": v(55.15, 14.38) * mm, "end": v(53.99, 18.61) * mm});
            skLineSegment(sketch, "E1005", {"start": v(53.99, 18.61) * mm, "end": v(52.53, 22.76) * mm});
            skLineSegment(sketch, "E1006", {"start": v(52.53, 22.76) * mm, "end": v(50.8, 26.79) * mm});
            skLineSegment(sketch, "E1007", {"start": v(50.8, 26.79) * mm, "end": v(48.77, 30.68) * mm});
            skLineSegment(sketch, "E1008", {"start": v(48.77, 30.68) * mm, "end": v(46.48, 34.43) * mm});
            skLineSegment(sketch, "E1009", {"start": v(46.48, 34.43) * mm, "end": v(43.94, 38) * mm});
            skLineSegment(sketch, "E1010", {"start": v(43.94, 38) * mm, "end": v(41.14, 41.4) * mm});
            skLineSegment(sketch, "E1011", {"start": v(41.14, 41.4) * mm, "end": v(38.12, 44.57) * mm});
            skLineSegment(sketch, "E1012", {"start": v(38.12, 44.57) * mm, "end": v(34.88, 47.54) * mm});
            skLineSegment(sketch, "E1013", {"start": v(34.88, 47.54) * mm, "end": v(31.44, 50.26) * mm});
            skLineSegment(sketch, "E1014", {"start": v(31.44, 50.26) * mm, "end": v(28.64, 49.67) * mm});
            skLineSegment(sketch, "E1015", {"start": v(28.64, 49.67) * mm, "end": v(5.75, 10.94) * mm});
            skLineSegment(sketch, "E1016", {"start": v(5.75, 10.94) * mm, "end": v(6.05, 7.29) * mm});
            skLineSegment(sketch, "E1017", {"start": v(6.05, 7.29) * mm, "end": v(9.63, 4.08) * mm});
            skLineSegment(sketch, "E1018", {"start": v(-1.53, 15.25) * mm, "end": v(21.36, 53.98) * mm});
            skLineSegment(sketch, "E1019", {"start": v(21.36, 53.98) * mm, "end": v(20.52, 56.72) * mm});
            skLineSegment(sketch, "E1020", {"start": v(20.52, 56.72) * mm, "end": v(16.47, 58.41) * mm});
            skLineSegment(sketch, "E1021", {"start": v(16.47, 58.41) * mm, "end": v(12.31, 59.82) * mm});
            skLineSegment(sketch, "E1022", {"start": v(12.31, 59.82) * mm, "end": v(8.07, 60.93) * mm});
            skLineSegment(sketch, "E1023", {"start": v(8.07, 60.93) * mm, "end": v(3.75, 61.74) * mm});
            skLineSegment(sketch, "E1024", {"start": v(3.75, 61.74) * mm, "end": v(-0.6, 62.25) * mm});
            skLineSegment(sketch, "E1025", {"start": v(-0.6, 62.25) * mm, "end": v(-5, 62.45) * mm});
            skLineSegment(sketch, "E1026", {"start": v(-5, 62.45) * mm, "end": v(-9.38, 62.34) * mm});
            skLineSegment(sketch, "E1027", {"start": v(-9.38, 62.34) * mm, "end": v(-13.75, 61.92) * mm});
            skLineSegment(sketch, "E1028", {"start": v(-13.75, 61.92) * mm, "end": v(-18.08, 61.2) * mm});
            skLineSegment(sketch, "E1029", {"start": v(-18.08, 61.2) * mm, "end": v(-22.35, 60.17) * mm});
            skLineSegment(sketch, "E1030", {"start": v(-22.35, 60.17) * mm, "end": v(-26.54, 58.85) * mm});
            skLineSegment(sketch, "E1031", {"start": v(-26.54, 58.85) * mm, "end": v(-30.62, 57.23) * mm});
            skLineSegment(sketch, "E1032", {"start": v(-30.62, 57.23) * mm, "end": v(-31.5, 54.5) * mm});
            skLineSegment(sketch, "E1033", {"start": v(-31.5, 54.5) * mm, "end": v(-9.4, 15.33) * mm});
            skLineSegment(sketch, "E1034", {"start": v(-9.4, 15.33) * mm, "end": v(-6.1, 13.75) * mm});
            skLineSegment(sketch, "E1035", {"start": v(-6.1, 13.75) * mm, "end": v(-1.53, 15.25) * mm});
            skLineSegment(sketch, "E1036", {"start": v(-16.77, 11.17) * mm, "end": v(-38.87, 50.35) * mm});
            skLineSegment(sketch, "E1037", {"start": v(-38.87, 50.35) * mm, "end": v(-41.67, 51) * mm});
            skLineSegment(sketch, "E1038", {"start": v(-41.67, 51) * mm, "end": v(-45.16, 48.34) * mm});
            skLineSegment(sketch, "E1039", {"start": v(-45.16, 48.34) * mm, "end": v(-48.46, 45.44) * mm});
            skLineSegment(sketch, "E1040", {"start": v(-48.46, 45.44) * mm, "end": v(-51.54, 42.32) * mm});
            skLineSegment(sketch, "E1041", {"start": v(-51.54, 42.32) * mm, "end": v(-54.4, 39) * mm});
            skLineSegment(sketch, "E1042", {"start": v(-54.4, 39) * mm, "end": v(-57.02, 35.47) * mm});
            skLineSegment(sketch, "E1043", {"start": v(-57.02, 35.47) * mm, "end": v(-59.39, 31.77) * mm});
            skLineSegment(sketch, "E1044", {"start": v(-59.39, 31.77) * mm, "end": v(-61.49, 27.91) * mm});
            skLineSegment(sketch, "E1045", {"start": v(-61.49, 27.91) * mm, "end": v(-63.3, 23.92) * mm});
            skLineSegment(sketch, "E1046", {"start": v(-63.3, 23.92) * mm, "end": v(-64.85, 19.8) * mm});
            skLineSegment(sketch, "E1047", {"start": v(-64.85, 19.8) * mm, "end": v(-66.1, 15.6) * mm});
            skLineSegment(sketch, "E1048", {"start": v(-66.1, 15.6) * mm, "end": v(-67.04, 11.31) * mm});
            skLineSegment(sketch, "E1049", {"start": v(-67.04, 11.31) * mm, "end": v(-67.68, 6.97) * mm});
            skLineSegment(sketch, "E1050", {"start": v(-67.68, 6.97) * mm, "end": v(-65.77, 4.84) * mm});
            skLineSegment(sketch, "E1051", {"start": v(-65.77, 4.84) * mm, "end": v(-20.78, 4.38) * mm});
            skLineSegment(sketch, "E1052", {"start": v(-20.78, 4.38) * mm, "end": v(-17.77, 6.47) * mm});
            skLineSegment(sketch, "E1053", {"start": v(-17.77, 6.47) * mm, "end": v(-16.77, 11.17) * mm});
            skLineSegment(sketch, "E1054", {"start": v(-20.87, -4.07) * mm, "end": v(-65.85, -3.62) * mm});
            skLineSegment(sketch, "E1055", {"start": v(-65.85, -3.62) * mm, "end": v(-67.8, -5.71) * mm});
            skLineSegment(sketch, "E1056", {"start": v(-67.8, -5.71) * mm, "end": v(-67.25, -10.07) * mm});
            skLineSegment(sketch, "E1057", {"start": v(-67.25, -10.07) * mm, "end": v(-66.4, -14.37) * mm});
            skLineSegment(sketch, "E1058", {"start": v(-66.4, -14.37) * mm, "end": v(-65.23, -18.6) * mm});
            skLineSegment(sketch, "E1059", {"start": v(-65.23, -18.6) * mm, "end": v(-63.78, -22.75) * mm});
            skLineSegment(sketch, "E1060", {"start": v(-63.78, -22.75) * mm, "end": v(-62.03, -26.78) * mm});
            skLineSegment(sketch, "E1061", {"start": v(-62.03, -26.78) * mm, "end": v(-60.01, -30.68) * mm});
            skLineSegment(sketch, "E1062", {"start": v(-60.01, -30.68) * mm, "end": v(-57.72, -34.42) * mm});
            skLineSegment(sketch, "E1063", {"start": v(-57.72, -34.42) * mm, "end": v(-55.18, -38) * mm});
            skLineSegment(sketch, "E1064", {"start": v(-55.18, -38) * mm, "end": v(-52.39, -41.38) * mm});
            skLineSegment(sketch, "E1065", {"start": v(-52.39, -41.38) * mm, "end": v(-49.36, -44.57) * mm});
            skLineSegment(sketch, "E1066", {"start": v(-49.36, -44.57) * mm, "end": v(-46.12, -47.53) * mm});
            skLineSegment(sketch, "E1067", {"start": v(-46.12, -47.53) * mm, "end": v(-42.68, -50.26) * mm});
            skLineSegment(sketch, "E1068", {"start": v(-42.68, -50.26) * mm, "end": v(-39.88, -49.67) * mm});
            skLineSegment(sketch, "E1069", {"start": v(-39.88, -49.67) * mm, "end": v(-17, -10.94) * mm});
            skLineSegment(sketch, "E1070", {"start": v(-17, -10.94) * mm, "end": v(-17.3, -7.28) * mm});
            skLineSegment(sketch, "E1071", {"start": v(-17.3, -7.28) * mm, "end": v(-20.87, -4.07) * mm});
            skLineSegment(sketch, "E1072", {"start": v(-9.72, -15.24) * mm, "end": v(-32.6, -53.97) * mm});
            skLineSegment(sketch, "E1073", {"start": v(-32.6, -53.97) * mm, "end": v(-31.76, -56.71) * mm});
            skLineSegment(sketch, "E1074", {"start": v(-31.76, -56.71) * mm, "end": v(-27.71, -58.4) * mm});
            skLineSegment(sketch, "E1075", {"start": v(-27.71, -58.4) * mm, "end": v(-23.56, -59.81) * mm});
            skLineSegment(sketch, "E1076", {"start": v(-23.56, -59.81) * mm, "end": v(-19.3, -60.93) * mm});
            skLineSegment(sketch, "E1077", {"start": v(-19.3, -60.93) * mm, "end": v(-15, -61.74) * mm});
            skLineSegment(sketch, "E1078", {"start": v(-15, -61.74) * mm, "end": v(-10.63, -62.24) * mm});
            skLineSegment(sketch, "E1079", {"start": v(-10.63, -62.24) * mm, "end": v(-6.25, -62.44) * mm});
            skLineSegment(sketch, "E1080", {"start": v(-6.25, -62.44) * mm, "end": v(-1.86, -62.33) * mm});
            skLineSegment(sketch, "E1081", {"start": v(-1.86, -62.33) * mm, "end": v(2.5, -61.91) * mm});
            skLineSegment(sketch, "E1082", {"start": v(2.5, -61.91) * mm, "end": v(6.84, -61.19) * mm});
            skLineSegment(sketch, "E1083", {"start": v(6.84, -61.19) * mm, "end": v(11.1, -60.16) * mm});
            skLineSegment(sketch, "E1084", {"start": v(11.1, -60.16) * mm, "end": v(15.3, -58.84) * mm});
            skLineSegment(sketch, "E1085", {"start": v(15.3, -58.84) * mm, "end": v(19.38, -57.22) * mm});
            skLineSegment(sketch, "E1086", {"start": v(19.38, -57.22) * mm, "end": v(20.27, -54.5) * mm});
            skLineSegment(sketch, "E1087", {"start": v(20.27, -54.5) * mm, "end": v(-1.83, -15.32) * mm});
            skLineSegment(sketch, "E1088", {"start": v(-1.83, -15.32) * mm, "end": v(-5.15, -13.75) * mm});
            skLineSegment(sketch, "E1089", {"start": v(-5.15, -13.75) * mm, "end": v(-9.72, -15.24) * mm});
            skLineSegment(sketch, "E1090", {"start": v(5.53, -11.16) * mm, "end": v(27.63, -50.35) * mm});
            skLineSegment(sketch, "E1091", {"start": v(27.63, -50.35) * mm, "end": v(30.42, -51) * mm});
            skLineSegment(sketch, "E1092", {"start": v(30.42, -51) * mm, "end": v(33.92, -48.33) * mm});
            skLineSegment(sketch, "E1093", {"start": v(33.92, -48.33) * mm, "end": v(37.22, -45.44) * mm});
            skLineSegment(sketch, "E1094", {"start": v(37.22, -45.44) * mm, "end": v(40.3, -42.32) * mm});
            skLineSegment(sketch, "E1095", {"start": v(40.3, -42.32) * mm, "end": v(43.16, -38.99) * mm});
            skLineSegment(sketch, "E1096", {"start": v(43.16, -38.99) * mm, "end": v(45.78, -35.46) * mm});
            skLineSegment(sketch, "E1097", {"start": v(45.78, -35.46) * mm, "end": v(48.14, -31.76) * mm});
            skLineSegment(sketch, "E1098", {"start": v(48.14, -31.76) * mm, "end": v(50.24, -27.9) * mm});
            skLineSegment(sketch, "E1099", {"start": v(50.24, -27.9) * mm, "end": v(52.07, -23.91) * mm});
            skLineSegment(sketch, "E1100", {"start": v(52.07, -23.91) * mm, "end": v(53.6, -19.8) * mm});
            skLineSegment(sketch, "E1101", {"start": v(53.6, -19.8) * mm, "end": v(54.85, -15.6) * mm});
            skLineSegment(sketch, "E1102", {"start": v(54.85, -15.6) * mm, "end": v(55.8, -11.3) * mm});
            skLineSegment(sketch, "E1103", {"start": v(55.8, -11.3) * mm, "end": v(56.44, -6.96) * mm});
            skLineSegment(sketch, "E1104", {"start": v(56.44, -6.96) * mm, "end": v(54.52, -4.83) * mm});
            skLineSegment(sketch, "E1105", {"start": v(54.52, -4.83) * mm, "end": v(9.54, -4.38) * mm});
            skLineSegment(sketch, "E1106", {"start": v(9.54, -4.38) * mm, "end": v(6.52, -6.46) * mm});
            skLineSegment(sketch, "E1107", {"start": v(6.52, -6.46) * mm, "end": v(5.53, -11.16) * mm});
            skLineSegment(sketch, "E1108", {"start": v(-4.62, 0) * mm, "end": v(-4.66, 0.26) * mm});
            skLineSegment(sketch, "E1109", {"start": v(-4.66, 0.26) * mm, "end": v(-4.76, 0.5) * mm});
            skLineSegment(sketch, "E1110", {"start": v(-4.76, 0.5) * mm, "end": v(-4.91, 0.71) * mm});
            skLineSegment(sketch, "E1111", {"start": v(-4.91, 0.71) * mm, "end": v(-5.12, 0.87) * mm});
            skLineSegment(sketch, "E1112", {"start": v(-5.12, 0.87) * mm, "end": v(-5.36, 0.97) * mm});
            skLineSegment(sketch, "E1113", {"start": v(-5.36, 0.97) * mm, "end": v(-5.62, 1) * mm});
            skLineSegment(sketch, "E1114", {"start": v(-5.62, 1) * mm, "end": v(-5.88, 0.97) * mm});
            skLineSegment(sketch, "E1115", {"start": v(-5.88, 0.97) * mm, "end": v(-6.12, 0.87) * mm});
            skLineSegment(sketch, "E1116", {"start": v(-6.12, 0.87) * mm, "end": v(-6.33, 0.71) * mm});
            skLineSegment(sketch, "E1117", {"start": v(-6.33, 0.71) * mm, "end": v(-6.49, 0.5) * mm});
            skLineSegment(sketch, "E1118", {"start": v(-6.49, 0.5) * mm, "end": v(-6.59, 0.26) * mm});
            skLineSegment(sketch, "E1119", {"start": v(-6.59, 0.26) * mm, "end": v(-6.62, 0) * mm});
            skLineSegment(sketch, "E1120", {"start": v(-6.62, 0) * mm, "end": v(-6.59, -0.26) * mm});
            skLineSegment(sketch, "E1121", {"start": v(-6.59, -0.26) * mm, "end": v(-6.49, -0.5) * mm});
            skLineSegment(sketch, "E1122", {"start": v(-6.49, -0.5) * mm, "end": v(-6.33, -0.7) * mm});
            skLineSegment(sketch, "E1123", {"start": v(-6.33, -0.7) * mm, "end": v(-6.12, -0.86) * mm});
            skLineSegment(sketch, "E1124", {"start": v(-6.12, -0.86) * mm, "end": v(-5.88, -0.96) * mm});
            skLineSegment(sketch, "E1125", {"start": v(-5.88, -0.96) * mm, "end": v(-5.62, -1) * mm});
            skLineSegment(sketch, "E1126", {"start": v(-5.62, -1) * mm, "end": v(-5.36, -0.96) * mm});
            skLineSegment(sketch, "E1127", {"start": v(-5.36, -0.96) * mm, "end": v(-5.12, -0.86) * mm});
            skLineSegment(sketch, "E1128", {"start": v(-5.12, -0.86) * mm, "end": v(-4.91, -0.7) * mm});
            skLineSegment(sketch, "E1129", {"start": v(-4.91, -0.7) * mm, "end": v(-4.76, -0.5) * mm});
            skLineSegment(sketch, "E1130", {"start": v(-4.76, -0.5) * mm, "end": v(-4.66, -0.26) * mm});
            skLineSegment(sketch, "E1131", {"start": v(-4.66, -0.26) * mm, "end": v(-4.62, 0) * mm});
            skLineSegment(sketch, "E1132", {"start": v(67.23, -0.11) * mm, "end": v(67.17, 0) * mm});
            skLineSegment(sketch, "E1133", {"start": v(67.17, 0) * mm, "end": v(67.12, 0.04) * mm});
            skLineSegment(sketch, "E1134", {"start": v(67.12, 0.04) * mm, "end": v(67, 0.09) * mm});
            skLineSegment(sketch, "E1135", {"start": v(67, 0.09) * mm, "end": v(66.9, 0.11) * mm});
            skLineSegment(sketch, "E1136", {"start": v(66.9, 0.11) * mm, "end": v(66.67, 0.1) * mm});
            skLineSegment(sketch, "E1137", {"start": v(66.67, 0.1) * mm, "end": v(66.45, 0.16) * mm});
            skLineSegment(sketch, "E1138", {"start": v(66.45, 0.16) * mm, "end": v(66.23, 0.26) * mm});
            skLineSegment(sketch, "E1139", {"start": v(66.23, 0.26) * mm, "end": v(66.01, 0.39) * mm});
            skLineSegment(sketch, "E1140", {"start": v(66.01, 0.39) * mm, "end": v(65.8, 0.55) * mm});
            skLineSegment(sketch, "E1141", {"start": v(65.8, 0.55) * mm, "end": v(65.6, 0.74) * mm});
            skLineSegment(sketch, "E1142", {"start": v(65.6, 0.74) * mm, "end": v(65.7, 1.24) * mm});
            skLineSegment(sketch, "E1143", {"start": v(65.7, 1.24) * mm, "end": v(65.84, 1.73) * mm});
            skLineSegment(sketch, "E1144", {"start": v(65.84, 1.73) * mm, "end": v(66.1, 1.8) * mm});
            skLineSegment(sketch, "E1145", {"start": v(66.1, 1.8) * mm, "end": v(66.36, 1.85) * mm});
            skLineSegment(sketch, "E1146", {"start": v(66.36, 1.85) * mm, "end": v(66.62, 1.87) * mm});
            skLineSegment(sketch, "E1147", {"start": v(66.62, 1.87) * mm, "end": v(66.86, 1.86) * mm});
            skLineSegment(sketch, "E1148", {"start": v(66.86, 1.86) * mm, "end": v(67.08, 1.8) * mm});
            skLineSegment(sketch, "E1149", {"start": v(67.08, 1.8) * mm, "end": v(67.28, 1.7) * mm});
            skLineSegment(sketch, "E1150", {"start": v(67.28, 1.7) * mm, "end": v(67.38, 1.67) * mm});
            skLineSegment(sketch, "E1151", {"start": v(67.38, 1.67) * mm, "end": v(67.5, 1.66) * mm});
            skLineSegment(sketch, "E1152", {"start": v(67.5, 1.66) * mm, "end": v(67.57, 1.67) * mm});
            skLineSegment(sketch, "E1153", {"start": v(67.57, 1.67) * mm, "end": v(67.68, 1.75) * mm});
            skLineSegment(sketch, "E1154", {"start": v(67.68, 1.75) * mm, "end": v(67.92, 2.13) * mm});
            skLineSegment(sketch, "E1155", {"start": v(67.92, 2.13) * mm, "end": v(68.2, 2.48) * mm});
            skLineSegment(sketch, "E1156", {"start": v(68.2, 2.48) * mm, "end": v(68.25, 2.6) * mm});
            skLineSegment(sketch, "E1157", {"start": v(68.25, 2.6) * mm, "end": v(68.24, 2.67) * mm});
            skLineSegment(sketch, "E1158", {"start": v(68.24, 2.67) * mm, "end": v(68.2, 2.78) * mm});
            skLineSegment(sketch, "E1159", {"start": v(68.2, 2.78) * mm, "end": v(68.13, 2.87) * mm});
            skLineSegment(sketch, "E1160", {"start": v(68.13, 2.87) * mm, "end": v(67.97, 3.03) * mm});
            skLineSegment(sketch, "E1161", {"start": v(67.97, 3.03) * mm, "end": v(67.84, 3.22) * mm});
            skLineSegment(sketch, "E1162", {"start": v(67.84, 3.22) * mm, "end": v(67.76, 3.45) * mm});
            skLineSegment(sketch, "E1163", {"start": v(67.76, 3.45) * mm, "end": v(67.7, 3.7) * mm});
            skLineSegment(sketch, "E1164", {"start": v(67.7, 3.7) * mm, "end": v(67.67, 3.96) * mm});
            skLineSegment(sketch, "E1165", {"start": v(67.67, 3.96) * mm, "end": v(67.66, 4.23) * mm});
            skLineSegment(sketch, "E1166", {"start": v(67.66, 4.23) * mm, "end": v(68.08, 4.52) * mm});
            skLineSegment(sketch, "E1167", {"start": v(68.08, 4.52) * mm, "end": v(68.52, 4.76) * mm});
            skLineSegment(sketch, "E1168", {"start": v(68.52, 4.76) * mm, "end": v(68.77, 4.63) * mm});
            skLineSegment(sketch, "E1169", {"start": v(68.77, 4.63) * mm, "end": v(68.98, 4.48) * mm});
            skLineSegment(sketch, "E1170", {"start": v(68.98, 4.48) * mm, "end": v(69.18, 4.32) * mm});
            skLineSegment(sketch, "E1171", {"start": v(69.18, 4.32) * mm, "end": v(69.34, 4.14) * mm});
            skLineSegment(sketch, "E1172", {"start": v(69.34, 4.14) * mm, "end": v(69.45, 3.94) * mm});
            skLineSegment(sketch, "E1173", {"start": v(69.45, 3.94) * mm, "end": v(69.52, 3.73) * mm});
            skLineSegment(sketch, "E1174", {"start": v(69.52, 3.73) * mm, "end": v(69.58, 3.63) * mm});
            skLineSegment(sketch, "E1175", {"start": v(69.58, 3.63) * mm, "end": v(69.65, 3.54) * mm});
            skLineSegment(sketch, "E1176", {"start": v(69.65, 3.54) * mm, "end": v(69.7, 3.5) * mm});
            skLineSegment(sketch, "E1177", {"start": v(69.7, 3.5) * mm, "end": v(69.84, 3.48) * mm});
            skLineSegment(sketch, "E1178", {"start": v(69.84, 3.48) * mm, "end": v(70.28, 3.58) * mm});
            skLineSegment(sketch, "E1179", {"start": v(70.28, 3.58) * mm, "end": v(70.73, 3.62) * mm});
            skLineSegment(sketch, "E1180", {"start": v(70.73, 3.62) * mm, "end": v(70.84, 3.68) * mm});
            skLineSegment(sketch, "E1181", {"start": v(70.84, 3.68) * mm, "end": v(70.89, 3.73) * mm});
            skLineSegment(sketch, "E1182", {"start": v(70.89, 3.73) * mm, "end": v(70.93, 3.84) * mm});
            skLineSegment(sketch, "E1183", {"start": v(70.93, 3.84) * mm, "end": v(70.95, 3.95) * mm});
            skLineSegment(sketch, "E1184", {"start": v(70.95, 3.95) * mm, "end": v(70.95, 4.18) * mm});
            skLineSegment(sketch, "E1185", {"start": v(70.95, 4.18) * mm, "end": v(71, 4.4) * mm});
            skLineSegment(sketch, "E1186", {"start": v(71, 4.4) * mm, "end": v(71.1, 4.62) * mm});
            skLineSegment(sketch, "E1187", {"start": v(71.1, 4.62) * mm, "end": v(71.23, 4.84) * mm});
            skLineSegment(sketch, "E1188", {"start": v(71.23, 4.84) * mm, "end": v(71.4, 5.05) * mm});
            skLineSegment(sketch, "E1189", {"start": v(71.4, 5.05) * mm, "end": v(71.58, 5.25) * mm});
            skLineSegment(sketch, "E1190", {"start": v(71.58, 5.25) * mm, "end": v(72.08, 5.15) * mm});
            skLineSegment(sketch, "E1191", {"start": v(72.08, 5.15) * mm, "end": v(72.57, 5.01) * mm});
            skLineSegment(sketch, "E1192", {"start": v(72.57, 5.01) * mm, "end": v(72.65, 4.74) * mm});
            skLineSegment(sketch, "E1193", {"start": v(72.65, 4.74) * mm, "end": v(72.7, 4.48) * mm});
            skLineSegment(sketch, "E1194", {"start": v(72.7, 4.48) * mm, "end": v(72.72, 4.23) * mm});
            skLineSegment(sketch, "E1195", {"start": v(72.72, 4.23) * mm, "end": v(72.7, 4) * mm});
            skLineSegment(sketch, "E1196", {"start": v(72.7, 4) * mm, "end": v(72.65, 3.77) * mm});
            skLineSegment(sketch, "E1197", {"start": v(72.65, 3.77) * mm, "end": v(72.54, 3.57) * mm});
            skLineSegment(sketch, "E1198", {"start": v(72.54, 3.57) * mm, "end": v(72.51, 3.46) * mm});
            skLineSegment(sketch, "E1199", {"start": v(72.51, 3.46) * mm, "end": v(72.5, 3.34) * mm});
            skLineSegment(sketch, "E1200", {"start": v(72.5, 3.34) * mm, "end": v(72.51, 3.28) * mm});
            skLineSegment(sketch, "E1201", {"start": v(72.51, 3.28) * mm, "end": v(72.6, 3.17) * mm});
            skLineSegment(sketch, "E1202", {"start": v(72.6, 3.17) * mm, "end": v(72.97, 2.93) * mm});
            skLineSegment(sketch, "E1203", {"start": v(72.97, 2.93) * mm, "end": v(73.32, 2.64) * mm});
            skLineSegment(sketch, "E1204", {"start": v(73.32, 2.64) * mm, "end": v(73.44, 2.6) * mm});
            skLineSegment(sketch, "E1205", {"start": v(73.44, 2.6) * mm, "end": v(73.51, 2.61) * mm});
            skLineSegment(sketch, "E1206", {"start": v(73.51, 2.61) * mm, "end": v(73.62, 2.66) * mm});
            skLineSegment(sketch, "E1207", {"start": v(73.62, 2.66) * mm, "end": v(73.71, 2.72) * mm});
            skLineSegment(sketch, "E1208", {"start": v(73.71, 2.72) * mm, "end": v(73.87, 2.88) * mm});
            skLineSegment(sketch, "E1209", {"start": v(73.87, 2.88) * mm, "end": v(74.06, 3) * mm});
            skLineSegment(sketch, "E1210", {"start": v(74.06, 3) * mm, "end": v(74.29, 3.09) * mm});
            skLineSegment(sketch, "E1211", {"start": v(74.29, 3.09) * mm, "end": v(74.53, 3.15) * mm});
            skLineSegment(sketch, "E1212", {"start": v(74.53, 3.15) * mm, "end": v(74.8, 3.18) * mm});
            skLineSegment(sketch, "E1213", {"start": v(74.8, 3.18) * mm, "end": v(75.07, 3.19) * mm});
            skLineSegment(sketch, "E1214", {"start": v(75.07, 3.19) * mm, "end": v(75.36, 2.77) * mm});
            skLineSegment(sketch, "E1215", {"start": v(75.36, 2.77) * mm, "end": v(75.6, 2.33) * mm});
            skLineSegment(sketch, "E1216", {"start": v(75.6, 2.33) * mm, "end": v(75.47, 2.08) * mm});
            skLineSegment(sketch, "E1217", {"start": v(75.47, 2.08) * mm, "end": v(75.32, 1.86) * mm});
            skLineSegment(sketch, "E1218", {"start": v(75.32, 1.86) * mm, "end": v(75.16, 1.67) * mm});
            skLineSegment(sketch, "E1219", {"start": v(75.16, 1.67) * mm, "end": v(74.98, 1.5) * mm});
            skLineSegment(sketch, "E1220", {"start": v(74.98, 1.5) * mm, "end": v(74.78, 1.4) * mm});
            skLineSegment(sketch, "E1221", {"start": v(74.78, 1.4) * mm, "end": v(74.57, 1.33) * mm});
            skLineSegment(sketch, "E1222", {"start": v(74.57, 1.33) * mm, "end": v(74.47, 1.27) * mm});
            skLineSegment(sketch, "E1223", {"start": v(74.47, 1.27) * mm, "end": v(74.38, 1.2) * mm});
            skLineSegment(sketch, "E1224", {"start": v(74.38, 1.2) * mm, "end": v(74.34, 1.14) * mm});
            skLineSegment(sketch, "E1225", {"start": v(74.34, 1.14) * mm, "end": v(74.32, 1) * mm});
            skLineSegment(sketch, "E1226", {"start": v(74.32, 1) * mm, "end": v(74.42, 0.57) * mm});
            skLineSegment(sketch, "E1227", {"start": v(74.42, 0.57) * mm, "end": v(74.46, 0.12) * mm});
            skLineSegment(sketch, "E1228", {"start": v(74.46, 0.12) * mm, "end": v(74.52, 0) * mm});
            skLineSegment(sketch, "E1229", {"start": v(74.52, 0) * mm, "end": v(74.57, -0.04) * mm});
            skLineSegment(sketch, "E1230", {"start": v(74.57, -0.04) * mm, "end": v(74.68, -0.08) * mm});
            skLineSegment(sketch, "E1231", {"start": v(74.68, -0.08) * mm, "end": v(74.8, -0.1) * mm});
            skLineSegment(sketch, "E1232", {"start": v(74.8, -0.1) * mm, "end": v(75.02, -0.1) * mm});
            skLineSegment(sketch, "E1233", {"start": v(75.02, -0.1) * mm, "end": v(75.24, -0.15) * mm});
            skLineSegment(sketch, "E1234", {"start": v(75.24, -0.15) * mm, "end": v(75.46, -0.25) * mm});
            skLineSegment(sketch, "E1235", {"start": v(75.46, -0.25) * mm, "end": v(75.68, -0.38) * mm});
            skLineSegment(sketch, "E1236", {"start": v(75.68, -0.38) * mm, "end": v(75.89, -0.54) * mm});
            skLineSegment(sketch, "E1237", {"start": v(75.89, -0.54) * mm, "end": v(76.09, -0.73) * mm});
            skLineSegment(sketch, "E1238", {"start": v(76.09, -0.73) * mm, "end": v(76, -1.23) * mm});
            skLineSegment(sketch, "E1239", {"start": v(76, -1.23) * mm, "end": v(75.85, -1.72) * mm});
            skLineSegment(sketch, "E1240", {"start": v(75.85, -1.72) * mm, "end": v(75.59, -1.8) * mm});
            skLineSegment(sketch, "E1241", {"start": v(75.59, -1.8) * mm, "end": v(75.33, -1.85) * mm});
            skLineSegment(sketch, "E1242", {"start": v(75.33, -1.85) * mm, "end": v(75.07, -1.87) * mm});
            skLineSegment(sketch, "E1243", {"start": v(75.07, -1.87) * mm, "end": v(74.83, -1.86) * mm});
            skLineSegment(sketch, "E1244", {"start": v(74.83, -1.86) * mm, "end": v(74.61, -1.8) * mm});
            skLineSegment(sketch, "E1245", {"start": v(74.61, -1.8) * mm, "end": v(74.41, -1.7) * mm});
            skLineSegment(sketch, "E1246", {"start": v(74.41, -1.7) * mm, "end": v(74.3, -1.66) * mm});
            skLineSegment(sketch, "E1247", {"start": v(74.3, -1.66) * mm, "end": v(74.19, -1.65) * mm});
            skLineSegment(sketch, "E1248", {"start": v(74.19, -1.65) * mm, "end": v(74.12, -1.66) * mm});
            skLineSegment(sketch, "E1249", {"start": v(74.12, -1.66) * mm, "end": v(74.01, -1.74) * mm});
            skLineSegment(sketch, "E1250", {"start": v(74.01, -1.74) * mm, "end": v(73.77, -2.12) * mm});
            skLineSegment(sketch, "E1251", {"start": v(73.77, -2.12) * mm, "end": v(73.48, -2.47) * mm});
            skLineSegment(sketch, "E1252", {"start": v(73.48, -2.47) * mm, "end": v(73.44, -2.6) * mm});
            skLineSegment(sketch, "E1253", {"start": v(73.44, -2.6) * mm, "end": v(73.45, -2.66) * mm});
            skLineSegment(sketch, "E1254", {"start": v(73.45, -2.66) * mm, "end": v(73.5, -2.77) * mm});
            skLineSegment(sketch, "E1255", {"start": v(73.5, -2.77) * mm, "end": v(73.56, -2.87) * mm});
            skLineSegment(sketch, "E1256", {"start": v(73.56, -2.87) * mm, "end": v(73.72, -3.02) * mm});
            skLineSegment(sketch, "E1257", {"start": v(73.72, -3.02) * mm, "end": v(73.85, -3.22) * mm});
            skLineSegment(sketch, "E1258", {"start": v(73.85, -3.22) * mm, "end": v(73.93, -3.44) * mm});
            skLineSegment(sketch, "E1259", {"start": v(73.93, -3.44) * mm, "end": v(73.99, -3.69) * mm});
            skLineSegment(sketch, "E1260", {"start": v(73.99, -3.69) * mm, "end": v(74.02, -3.95) * mm});
            skLineSegment(sketch, "E1261", {"start": v(74.02, -3.95) * mm, "end": v(74.03, -4.23) * mm});
            skLineSegment(sketch, "E1262", {"start": v(74.03, -4.23) * mm, "end": v(73.61, -4.51) * mm});
            skLineSegment(sketch, "E1263", {"start": v(73.61, -4.51) * mm, "end": v(73.17, -4.76) * mm});
            skLineSegment(sketch, "E1264", {"start": v(73.17, -4.76) * mm, "end": v(72.92, -4.62) * mm});
            skLineSegment(sketch, "E1265", {"start": v(72.92, -4.62) * mm, "end": v(72.7, -4.47) * mm});
            skLineSegment(sketch, "E1266", {"start": v(72.7, -4.47) * mm, "end": v(72.51, -4.3) * mm});
            skLineSegment(sketch, "E1267", {"start": v(72.51, -4.3) * mm, "end": v(72.35, -4.13) * mm});
            skLineSegment(sketch, "E1268", {"start": v(72.35, -4.13) * mm, "end": v(72.24, -3.93) * mm});
            skLineSegment(sketch, "E1269", {"start": v(72.24, -3.93) * mm, "end": v(72.17, -3.72) * mm});
            skLineSegment(sketch, "E1270", {"start": v(72.17, -3.72) * mm, "end": v(72.11, -3.62) * mm});
            skLineSegment(sketch, "E1271", {"start": v(72.11, -3.62) * mm, "end": v(72.04, -3.53) * mm});
            skLineSegment(sketch, "E1272", {"start": v(72.04, -3.53) * mm, "end": v(71.98, -3.49) * mm});
            skLineSegment(sketch, "E1273", {"start": v(71.98, -3.49) * mm, "end": v(71.85, -3.47) * mm});
            skLineSegment(sketch, "E1274", {"start": v(71.85, -3.47) * mm, "end": v(71.41, -3.57) * mm});
            skLineSegment(sketch, "E1275", {"start": v(71.41, -3.57) * mm, "end": v(70.96, -3.61) * mm});
            skLineSegment(sketch, "E1276", {"start": v(70.96, -3.61) * mm, "end": v(70.84, -3.67) * mm});
            skLineSegment(sketch, "E1277", {"start": v(70.84, -3.67) * mm, "end": v(70.8, -3.73) * mm});
            skLineSegment(sketch, "E1278", {"start": v(70.8, -3.73) * mm, "end": v(70.76, -3.84) * mm});
            skLineSegment(sketch, "E1279", {"start": v(70.76, -3.84) * mm, "end": v(70.74, -3.95) * mm});
            skLineSegment(sketch, "E1280", {"start": v(70.74, -3.95) * mm, "end": v(70.74, -4.17) * mm});
            skLineSegment(sketch, "E1281", {"start": v(70.74, -4.17) * mm, "end": v(70.7, -4.4) * mm});
            skLineSegment(sketch, "E1282", {"start": v(70.7, -4.4) * mm, "end": v(70.6, -4.61) * mm});
            skLineSegment(sketch, "E1283", {"start": v(70.6, -4.61) * mm, "end": v(70.46, -4.83) * mm});
            skLineSegment(sketch, "E1284", {"start": v(70.46, -4.83) * mm, "end": v(70.3, -5.04) * mm});
            skLineSegment(sketch, "E1285", {"start": v(70.3, -5.04) * mm, "end": v(70.1, -5.24) * mm});
            skLineSegment(sketch, "E1286", {"start": v(70.1, -5.24) * mm, "end": v(69.6, -5.15) * mm});
            skLineSegment(sketch, "E1287", {"start": v(69.6, -5.15) * mm, "end": v(69.12, -5) * mm});
            skLineSegment(sketch, "E1288", {"start": v(69.12, -5) * mm, "end": v(69.04, -4.74) * mm});
            skLineSegment(sketch, "E1289", {"start": v(69.04, -4.74) * mm, "end": v(69, -4.48) * mm});
            skLineSegment(sketch, "E1290", {"start": v(69, -4.48) * mm, "end": v(68.97, -4.23) * mm});
            skLineSegment(sketch, "E1291", {"start": v(68.97, -4.23) * mm, "end": v(68.99, -3.98) * mm});
            skLineSegment(sketch, "E1292", {"start": v(68.99, -3.98) * mm, "end": v(69.04, -3.77) * mm});
            skLineSegment(sketch, "E1293", {"start": v(69.04, -3.77) * mm, "end": v(69.15, -3.57) * mm});
            skLineSegment(sketch, "E1294", {"start": v(69.15, -3.57) * mm, "end": v(69.18, -3.46) * mm});
            skLineSegment(sketch, "E1295", {"start": v(69.18, -3.46) * mm, "end": v(69.19, -3.34) * mm});
            skLineSegment(sketch, "E1296", {"start": v(69.19, -3.34) * mm, "end": v(69.18, -3.27) * mm});
            skLineSegment(sketch, "E1297", {"start": v(69.18, -3.27) * mm, "end": v(69.1, -3.16) * mm});
            skLineSegment(sketch, "E1298", {"start": v(69.1, -3.16) * mm, "end": v(68.72, -2.92) * mm});
            skLineSegment(sketch, "E1299", {"start": v(68.72, -2.92) * mm, "end": v(68.37, -2.64) * mm});
            skLineSegment(sketch, "E1300", {"start": v(68.37, -2.64) * mm, "end": v(68.25, -2.6) * mm});
            skLineSegment(sketch, "E1301", {"start": v(68.25, -2.6) * mm, "end": v(68.18, -2.6) * mm});
            skLineSegment(sketch, "E1302", {"start": v(68.18, -2.6) * mm, "end": v(68.07, -2.65) * mm});
            skLineSegment(sketch, "E1303", {"start": v(68.07, -2.65) * mm, "end": v(67.97, -2.71) * mm});
            skLineSegment(sketch, "E1304", {"start": v(67.97, -2.71) * mm, "end": v(67.82, -2.87) * mm});
            skLineSegment(sketch, "E1305", {"start": v(67.82, -2.87) * mm, "end": v(67.63, -3) * mm});
            skLineSegment(sketch, "E1306", {"start": v(67.63, -3) * mm, "end": v(67.4, -3.08) * mm});
            skLineSegment(sketch, "E1307", {"start": v(67.4, -3.08) * mm, "end": v(67.15, -3.14) * mm});
            skLineSegment(sketch, "E1308", {"start": v(67.15, -3.14) * mm, "end": v(66.9, -3.17) * mm});
            skLineSegment(sketch, "E1309", {"start": v(66.9, -3.17) * mm, "end": v(66.61, -3.18) * mm});
            skLineSegment(sketch, "E1310", {"start": v(66.61, -3.18) * mm, "end": v(66.33, -2.76) * mm});
            skLineSegment(sketch, "E1311", {"start": v(66.33, -2.76) * mm, "end": v(66.09, -2.32) * mm});
            skLineSegment(sketch, "E1312", {"start": v(66.09, -2.32) * mm, "end": v(66.22, -2.08) * mm});
            skLineSegment(sketch, "E1313", {"start": v(66.22, -2.08) * mm, "end": v(66.37, -1.86) * mm});
            skLineSegment(sketch, "E1314", {"start": v(66.37, -1.86) * mm, "end": v(66.53, -1.66) * mm});
            skLineSegment(sketch, "E1315", {"start": v(66.53, -1.66) * mm, "end": v(66.7, -1.5) * mm});
            skLineSegment(sketch, "E1316", {"start": v(66.7, -1.5) * mm, "end": v(66.9, -1.39) * mm});
            skLineSegment(sketch, "E1317", {"start": v(66.9, -1.39) * mm, "end": v(67.12, -1.32) * mm});
            skLineSegment(sketch, "E1318", {"start": v(67.12, -1.32) * mm, "end": v(67.22, -1.27) * mm});
            skLineSegment(sketch, "E1319", {"start": v(67.22, -1.27) * mm, "end": v(67.31, -1.19) * mm});
            skLineSegment(sketch, "E1320", {"start": v(67.31, -1.19) * mm, "end": v(67.35, -1.13) * mm});
            skLineSegment(sketch, "E1321", {"start": v(67.35, -1.13) * mm, "end": v(67.37, -1) * mm});
            skLineSegment(sketch, "E1322", {"start": v(67.37, -1) * mm, "end": v(67.27, -0.56) * mm});
            skLineSegment(sketch, "E1323", {"start": v(67.27, -0.56) * mm, "end": v(67.23, -0.11) * mm});
            skLineSegment(sketch, "E1324", {"start": v(71.6, 0) * mm, "end": v(71.57, 0.2) * mm});
            skLineSegment(sketch, "E1325", {"start": v(71.57, 0.2) * mm, "end": v(71.5, 0.38) * mm});
            skLineSegment(sketch, "E1326", {"start": v(71.5, 0.38) * mm, "end": v(71.38, 0.53) * mm});
            skLineSegment(sketch, "E1327", {"start": v(71.38, 0.53) * mm, "end": v(71.22, 0.65) * mm});
            skLineSegment(sketch, "E1328", {"start": v(71.22, 0.65) * mm, "end": v(71.04, 0.73) * mm});
            skLineSegment(sketch, "E1329", {"start": v(71.04, 0.73) * mm, "end": v(70.84, 0.75) * mm});
            skLineSegment(sketch, "E1330", {"start": v(70.84, 0.75) * mm, "end": v(70.65, 0.73) * mm});
            skLineSegment(sketch, "E1331", {"start": v(70.65, 0.73) * mm, "end": v(70.47, 0.65) * mm});
            skLineSegment(sketch, "E1332", {"start": v(70.47, 0.65) * mm, "end": v(70.31, 0.53) * mm});
            skLineSegment(sketch, "E1333", {"start": v(70.31, 0.53) * mm, "end": v(70.2, 0.38) * mm});
            skLineSegment(sketch, "E1334", {"start": v(70.2, 0.38) * mm, "end": v(70.12, 0.2) * mm});
            skLineSegment(sketch, "E1335", {"start": v(70.12, 0.2) * mm, "end": v(70.1, 0) * mm});
            skLineSegment(sketch, "E1336", {"start": v(70.1, 0) * mm, "end": v(70.12, -0.2) * mm});
            skLineSegment(sketch, "E1337", {"start": v(70.12, -0.2) * mm, "end": v(70.2, -0.37) * mm});
            skLineSegment(sketch, "E1338", {"start": v(70.2, -0.37) * mm, "end": v(70.31, -0.53) * mm});
            skLineSegment(sketch, "E1339", {"start": v(70.31, -0.53) * mm, "end": v(70.47, -0.65) * mm});
            skLineSegment(sketch, "E1340", {"start": v(70.47, -0.65) * mm, "end": v(70.65, -0.72) * mm});
            skLineSegment(sketch, "E1341", {"start": v(70.65, -0.72) * mm, "end": v(70.84, -0.75) * mm});
            skLineSegment(sketch, "E1342", {"start": v(70.84, -0.75) * mm, "end": v(71.04, -0.72) * mm});
            skLineSegment(sketch, "E1343", {"start": v(71.04, -0.72) * mm, "end": v(71.22, -0.65) * mm});
            skLineSegment(sketch, "E1344", {"start": v(71.22, -0.65) * mm, "end": v(71.38, -0.53) * mm});
            skLineSegment(sketch, "E1345", {"start": v(71.38, -0.53) * mm, "end": v(71.5, -0.37) * mm});
            skLineSegment(sketch, "E1346", {"start": v(71.5, -0.37) * mm, "end": v(71.57, -0.2) * mm});
            skLineSegment(sketch, "E1347", {"start": v(71.57, -0.2) * mm, "end": v(71.6, 0) * mm});
            skSolve(sketch);
        }
        {
            var Q0;
            Q0=makeQuery(id+"F0.imprint","IMPRINT",FACE,{"disambiguationData":[TD([[makeQuery(id+"F0.imprint","IMPRINT",EDGE,{"derivedFrom":sQuery(id+"F0.wireOp",EDGE,"E0")}),-1.0]])]});
            var Q1;
            Q1=makeQuery(id+"F0.imprint","IMPRINT",FACE,{"disambiguationData":[TD([[makeQuery(id+"F0.imprint","IMPRINT",EDGE,{"derivedFrom":sQuery(id+"F0.wireOp",EDGE,"E1132")}),-1.0]])]});
            extrude(context, id + "F1", {"entities" : qUnion([Q0, Q1]), "depth" : 4 * mm, "offsetDistance" : 25 * mm});
        }
    });
